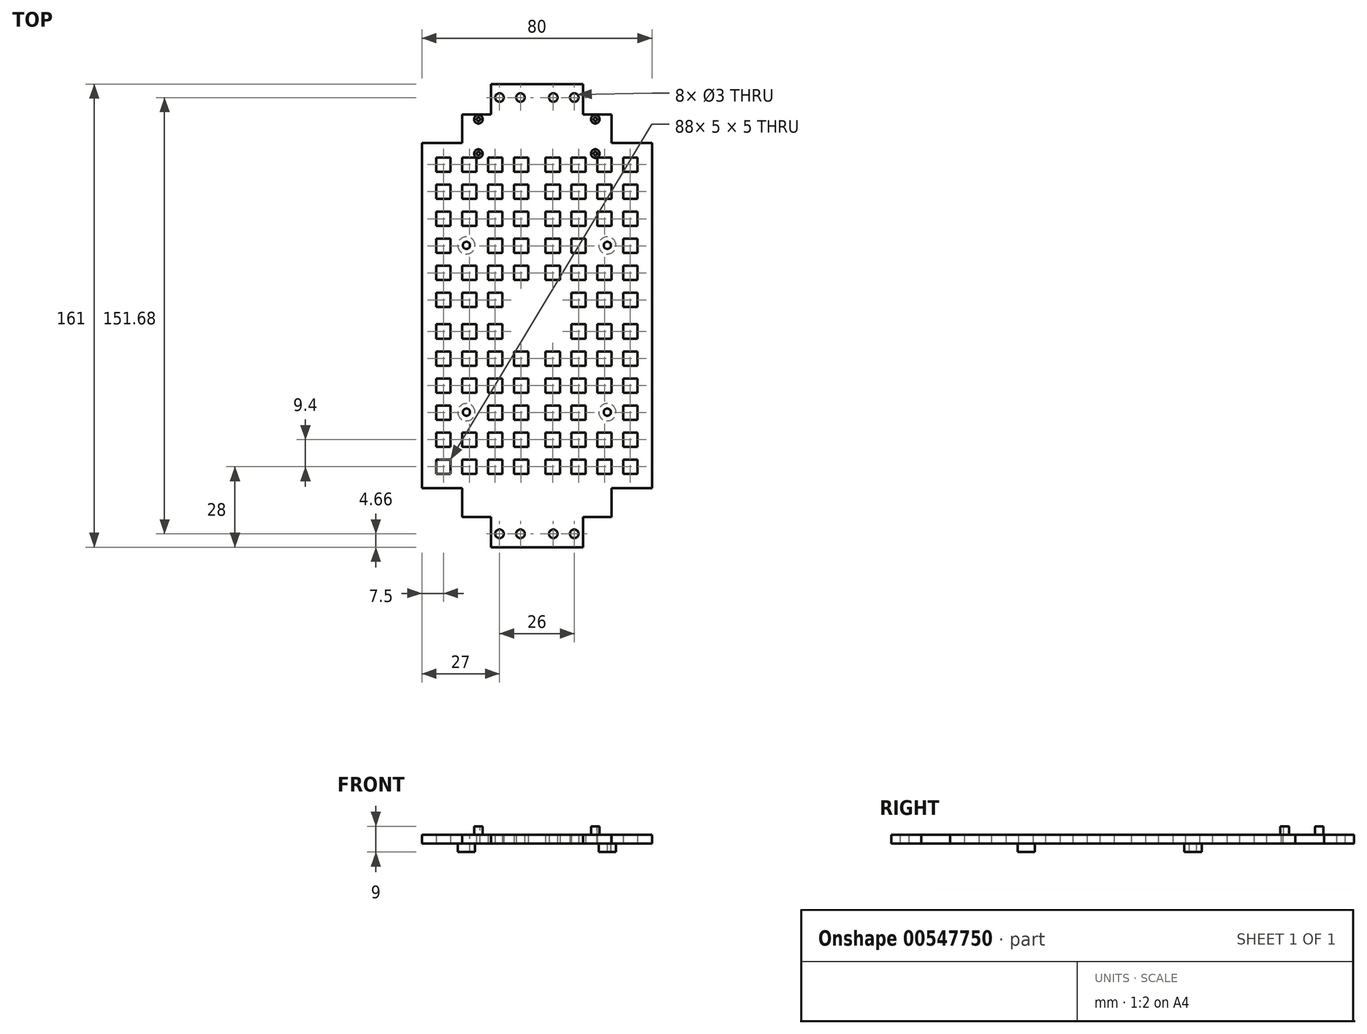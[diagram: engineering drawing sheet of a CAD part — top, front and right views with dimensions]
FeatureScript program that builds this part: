
annotation { "Feature Type Name" : "Feature", "Feature Type Description" : "" }
export const myFeature = defineFeature(function(context is Context, id is Id, definition is map)
    precondition{}
    {
        {
            var Q0;
            Q0=qCreatedBy(makeId("Top.planeOp"),FACE);
            var sketch = newSketch(context, id + "F0", { "sketchPlane" : qUnion([Q0])});
            skLineSegment(sketch, "E0", {"start": v(0, 0) * mm, "end": v(0, 77.06) * mm, "construction": true});
            skLineSegment(sketch, "E1", {"start": v(0, 0) * mm, "end": v(51.76, 0) * mm, "construction": true});
            skLineSegment(sketch, "E2", {"start": v(0, 80.5) * mm, "end": v(16, 80.5) * mm});
            skLineSegment(sketch, "E3", {"start": v(16, 80.5) * mm, "end": v(16, 70) * mm});
            skLineSegment(sketch, "E4", {"start": v(26, 60) * mm, "end": v(40, 60) * mm});
            skLineSegment(sketch, "E5", {"start": v(40, 60) * mm, "end": v(40, 0) * mm});
            skLineSegment(sketch, "E6.MirrorCS", {"start": v(-40, 60) * mm, "end": v(-40, 0) * mm});
            skLineSegment(sketch, "E7.MirrorCS", {"start": v(-26, 60) * mm, "end": v(-40, 60) * mm});
            skLineSegment(sketch, "E8.MirrorCS", {"start": v(0, 80.5) * mm, "end": v(-16, 80.5) * mm});
            skLineSegment(sketch, "E9.MirrorCS", {"start": v(40, -60) * mm, "end": v(40, 0) * mm});
            skLineSegment(sketch, "E10.MirrorCS", {"start": v(-40, -60) * mm, "end": v(-40, 0) * mm});
            skCircle(sketch, "E11", {"center": v(5.7, 75.84) * mm, "radius": 1.5 * mm});
            skCircle(sketch, "E12", {"center": v(13, 75.84) * mm, "radius": 1.5 * mm});
            skLineSegment(sketch, "E13", {"start": v(0, 75.84) * mm, "end": v(16, 75.84) * mm, "construction": true});
            skCircle(sketch, "E14.MirrorC", {"center": v(-13, 75.84) * mm, "radius": 1.5 * mm});
            skCircle(sketch, "E15.MirrorC", {"center": v(-5.7, 75.84) * mm, "radius": 1.5 * mm});
            skLineSegment(sketch, "E16", {"start": v(16, 70) * mm, "end": v(26, 70) * mm});
            skLineSegment(sketch, "E17", {"start": v(26, 70) * mm, "end": v(26, 60) * mm});
            skLineSegment(sketch, "E18.MirrorCS", {"start": v(-26, 70) * mm, "end": v(-26, 60) * mm});
            skLineSegment(sketch, "E19.MirrorCS", {"start": v(-16, 80.5) * mm, "end": v(-16, 70) * mm});
            skLineSegment(sketch, "E20.MirrorCS", {"start": v(-16, 70) * mm, "end": v(-26, 70) * mm});
            skLineSegment(sketch, "E21.MirrorCS", {"start": v(-26, -60) * mm, "end": v(-40, -60) * mm});
            skLineSegment(sketch, "E22.MirrorCS", {"start": v(26, -60) * mm, "end": v(40, -60) * mm});
            skLineSegment(sketch, "E23.MirrorCS", {"start": v(26, -70) * mm, "end": v(26, -60) * mm});
            skLineSegment(sketch, "E24.MirrorCS", {"start": v(16, -70) * mm, "end": v(26, -70) * mm});
            skLineSegment(sketch, "E25.MirrorCS", {"start": v(16, -80.5) * mm, "end": v(16, -70) * mm});
            skLineSegment(sketch, "E26.MirrorCS", {"start": v(0, -80.5) * mm, "end": v(16, -80.5) * mm});
            skLineSegment(sketch, "E27.MirrorCS", {"start": v(0, -80.5) * mm, "end": v(-16, -80.5) * mm});
            skLineSegment(sketch, "E28.MirrorCS", {"start": v(-16, -80.5) * mm, "end": v(-16, -70) * mm});
            skLineSegment(sketch, "E29.MirrorCS", {"start": v(-26, -70) * mm, "end": v(-26, -60) * mm});
            skLineSegment(sketch, "E30.MirrorCS", {"start": v(-16, -70) * mm, "end": v(-26, -70) * mm});
            skCircle(sketch, "E31.MirrorC", {"center": v(13, -75.84) * mm, "radius": 1.5 * mm});
            skCircle(sketch, "E32.MirrorC", {"center": v(5.7, -75.84) * mm, "radius": 1.5 * mm});
            skCircle(sketch, "E33.MirrorC", {"center": v(-13, -75.84) * mm, "radius": 1.5 * mm});
            skCircle(sketch, "E34.MirrorC", {"center": v(-5.7, -75.84) * mm, "radius": 1.5 * mm});
            skLineSegment(sketch, "E35.bottom", {"start": v(35, 50) * mm, "end": v(30, 50) * mm});
            skLineSegment(sketch, "E35.top", {"start": v(35, 55) * mm, "end": v(30, 55) * mm});
            skLineSegment(sketch, "E35.left", {"start": v(35, 50) * mm, "end": v(35, 55) * mm});
            skLineSegment(sketch, "E35.right", {"start": v(30, 50) * mm, "end": v(30, 55) * mm});
            skPoint(sketch, "E35.middle", {"position": v(32.5, 52.5) * mm});
            skPoint(sketch, "E36.1.0.0", {"position": v(23.5, 52.5) * mm});
            skLineSegment(sketch, "E36.1.0.1", {"start": v(26, 55) * mm, "end": v(21, 55) * mm});
            skLineSegment(sketch, "E36.1.0.2", {"start": v(26, 50) * mm, "end": v(21, 50) * mm});
            skLineSegment(sketch, "E36.1.0.3", {"start": v(21, 50) * mm, "end": v(21, 55) * mm});
            skLineSegment(sketch, "E36.1.0.4", {"start": v(26, 50) * mm, "end": v(26, 55) * mm});
            skPoint(sketch, "E36.2.0.0", {"position": v(14.5, 52.5) * mm});
            skLineSegment(sketch, "E36.2.0.1", {"start": v(17, 55) * mm, "end": v(12, 55) * mm});
            skLineSegment(sketch, "E36.2.0.2", {"start": v(17, 50) * mm, "end": v(12, 50) * mm});
            skLineSegment(sketch, "E36.2.0.3", {"start": v(12, 50) * mm, "end": v(12, 55) * mm});
            skLineSegment(sketch, "E36.2.0.4", {"start": v(17, 50) * mm, "end": v(17, 55) * mm});
            skLineSegment(sketch, "E36.direction1", {"start": v(30, 50) * mm, "end": v(21, 50) * mm, "construction": true});
            skPoint(sketch, "E37.0.3.0", {"position": v(5.5, 52.5) * mm});
            skLineSegment(sketch, "E37.1.3.0", {"start": v(8, 55) * mm, "end": v(3, 55) * mm});
            skLineSegment(sketch, "E37.4.3.0", {"start": v(8, 50) * mm, "end": v(3, 50) * mm});
            skLineSegment(sketch, "E37.7.3.0", {"start": v(3, 50) * mm, "end": v(3, 55) * mm});
            skLineSegment(sketch, "E37.10.3.0", {"start": v(8, 50) * mm, "end": v(8, 55) * mm});
            skLineSegment(sketch, "E38.1.0.0", {"start": v(17, 40.6) * mm, "end": v(17, 45.6) * mm});
            skLineSegment(sketch, "E38.1.0.1", {"start": v(3, 40.6) * mm, "end": v(3, 45.6) * mm});
            skLineSegment(sketch, "E38.1.0.2", {"start": v(21, 40.6) * mm, "end": v(21, 45.6) * mm});
            skPoint(sketch, "E38.1.0.3", {"position": v(5.5, 43.1) * mm});
            skLineSegment(sketch, "E38.1.0.4", {"start": v(26, 40.6) * mm, "end": v(26, 45.6) * mm});
            skLineSegment(sketch, "E38.1.0.5", {"start": v(30, 40.6) * mm, "end": v(21, 40.6) * mm, "construction": true});
            skLineSegment(sketch, "E38.1.0.6", {"start": v(35, 45.6) * mm, "end": v(30, 45.6) * mm});
            skLineSegment(sketch, "E38.1.0.7", {"start": v(35, 40.6) * mm, "end": v(35, 45.6) * mm});
            skLineSegment(sketch, "E38.1.0.8", {"start": v(12, 40.6) * mm, "end": v(12, 45.6) * mm});
            skLineSegment(sketch, "E38.1.0.9", {"start": v(17, 40.6) * mm, "end": v(12, 40.6) * mm});
            skPoint(sketch, "E38.1.0.10", {"position": v(23.5, 43.1) * mm});
            skLineSegment(sketch, "E38.1.0.11", {"start": v(8, 40.6) * mm, "end": v(8, 45.6) * mm});
            skLineSegment(sketch, "E38.1.0.12", {"start": v(26, 45.6) * mm, "end": v(21, 45.6) * mm});
            skLineSegment(sketch, "E38.1.0.13", {"start": v(17, 45.6) * mm, "end": v(12, 45.6) * mm});
            skPoint(sketch, "E38.1.0.14", {"position": v(14.5, 43.1) * mm});
            skLineSegment(sketch, "E38.1.0.15", {"start": v(8, 40.6) * mm, "end": v(3, 40.6) * mm});
            skLineSegment(sketch, "E38.1.0.16", {"start": v(35, 40.6) * mm, "end": v(30, 40.6) * mm});
            skPoint(sketch, "E38.1.0.17", {"position": v(32.5, 43.1) * mm});
            skLineSegment(sketch, "E38.1.0.18", {"start": v(8, 45.6) * mm, "end": v(3, 45.6) * mm});
            skLineSegment(sketch, "E38.1.0.19", {"start": v(30, 40.6) * mm, "end": v(30, 45.6) * mm});
            skLineSegment(sketch, "E38.1.0.20", {"start": v(26, 40.6) * mm, "end": v(21, 40.6) * mm});
            skLineSegment(sketch, "E38.2.0.0", {"start": v(17, 31.2) * mm, "end": v(17, 36.2) * mm});
            skLineSegment(sketch, "E38.2.0.1", {"start": v(3, 31.2) * mm, "end": v(3, 36.2) * mm});
            skLineSegment(sketch, "E38.2.0.2", {"start": v(21, 31.2) * mm, "end": v(21, 36.2) * mm});
            skPoint(sketch, "E38.2.0.3", {"position": v(5.5, 33.7) * mm});
            skLineSegment(sketch, "E38.2.0.4", {"start": v(26, 31.2) * mm, "end": v(26, 36.2) * mm});
            skLineSegment(sketch, "E38.2.0.5", {"start": v(30, 31.2) * mm, "end": v(21, 31.2) * mm, "construction": true});
            skLineSegment(sketch, "E38.2.0.6", {"start": v(35, 36.2) * mm, "end": v(30, 36.2) * mm});
            skLineSegment(sketch, "E38.2.0.7", {"start": v(35, 31.2) * mm, "end": v(35, 36.2) * mm});
            skLineSegment(sketch, "E38.2.0.8", {"start": v(12, 31.2) * mm, "end": v(12, 36.2) * mm});
            skLineSegment(sketch, "E38.2.0.9", {"start": v(17, 31.2) * mm, "end": v(12, 31.2) * mm});
            skPoint(sketch, "E38.2.0.10", {"position": v(23.5, 33.7) * mm});
            skLineSegment(sketch, "E38.2.0.11", {"start": v(8, 31.2) * mm, "end": v(8, 36.2) * mm});
            skLineSegment(sketch, "E38.2.0.12", {"start": v(26, 36.2) * mm, "end": v(21, 36.2) * mm});
            skLineSegment(sketch, "E38.2.0.13", {"start": v(17, 36.2) * mm, "end": v(12, 36.2) * mm});
            skPoint(sketch, "E38.2.0.14", {"position": v(14.5, 33.7) * mm});
            skLineSegment(sketch, "E38.2.0.15", {"start": v(8, 31.2) * mm, "end": v(3, 31.2) * mm});
            skLineSegment(sketch, "E38.2.0.16", {"start": v(35, 31.2) * mm, "end": v(30, 31.2) * mm});
            skPoint(sketch, "E38.2.0.17", {"position": v(32.5, 33.7) * mm});
            skLineSegment(sketch, "E38.2.0.18", {"start": v(8, 36.2) * mm, "end": v(3, 36.2) * mm});
            skLineSegment(sketch, "E38.2.0.19", {"start": v(30, 31.2) * mm, "end": v(30, 36.2) * mm});
            skLineSegment(sketch, "E38.2.0.20", {"start": v(26, 31.2) * mm, "end": v(21, 31.2) * mm});
            skLineSegment(sketch, "E38.direction1", {"start": v(3, 50) * mm, "end": v(3, 40.6) * mm, "construction": true});
            skLineSegment(sketch, "E39.0.3.0", {"start": v(17, 21.8) * mm, "end": v(17, 26.8) * mm});
            skLineSegment(sketch, "E39.3.3.0", {"start": v(3, 21.8) * mm, "end": v(3, 26.8) * mm});
            skLineSegment(sketch, "E39.6.3.0", {"start": v(21, 21.8) * mm, "end": v(21, 26.8) * mm, "construction": true});
            skPoint(sketch, "E39.9.3.0", {"position": v(5.5, 24.3) * mm});
            skLineSegment(sketch, "E39.10.3.0", {"start": v(26, 21.8) * mm, "end": v(26, 26.8) * mm, "construction": true});
            skLineSegment(sketch, "E39.13.3.0", {"start": v(30, 21.8) * mm, "end": v(21, 21.8) * mm, "construction": true});
            skLineSegment(sketch, "E39.16.3.0", {"start": v(35, 26.8) * mm, "end": v(30, 26.8) * mm});
            skLineSegment(sketch, "E39.19.3.0", {"start": v(35, 21.8) * mm, "end": v(35, 26.8) * mm});
            skLineSegment(sketch, "E39.22.3.0", {"start": v(12, 21.8) * mm, "end": v(12, 26.8) * mm});
            skLineSegment(sketch, "E39.25.3.0", {"start": v(17, 21.8) * mm, "end": v(12, 21.8) * mm});
            skPoint(sketch, "E39.28.3.0", {"position": v(23.5, 24.3) * mm});
            skLineSegment(sketch, "E39.29.3.0", {"start": v(8, 21.8) * mm, "end": v(8, 26.8) * mm});
            skLineSegment(sketch, "E39.32.3.0", {"start": v(26, 26.8) * mm, "end": v(21, 26.8) * mm, "construction": true});
            skLineSegment(sketch, "E39.35.3.0", {"start": v(17, 26.8) * mm, "end": v(12, 26.8) * mm});
            skPoint(sketch, "E39.38.3.0", {"position": v(14.5, 24.3) * mm});
            skLineSegment(sketch, "E39.39.3.0", {"start": v(8, 21.8) * mm, "end": v(3, 21.8) * mm});
            skLineSegment(sketch, "E39.42.3.0", {"start": v(35, 21.8) * mm, "end": v(30, 21.8) * mm});
            skPoint(sketch, "E39.45.3.0", {"position": v(32.5, 24.3) * mm});
            skLineSegment(sketch, "E39.46.3.0", {"start": v(8, 26.8) * mm, "end": v(3, 26.8) * mm});
            skLineSegment(sketch, "E39.49.3.0", {"start": v(30, 21.8) * mm, "end": v(30, 26.8) * mm});
            skLineSegment(sketch, "E39.52.3.0", {"start": v(26, 21.8) * mm, "end": v(21, 21.8) * mm, "construction": true});
            skLineSegment(sketch, "E39.0.4.0", {"start": v(17, 12.4) * mm, "end": v(17, 17.4) * mm});
            skLineSegment(sketch, "E39.3.4.0", {"start": v(3, 12.4) * mm, "end": v(3, 17.4) * mm});
            skLineSegment(sketch, "E39.6.4.0", {"start": v(21, 12.4) * mm, "end": v(21, 17.4) * mm});
            skPoint(sketch, "E39.9.4.0", {"position": v(5.5, 14.9) * mm});
            skLineSegment(sketch, "E39.10.4.0", {"start": v(26, 12.4) * mm, "end": v(26, 17.4) * mm});
            skLineSegment(sketch, "E39.13.4.0", {"start": v(30, 12.4) * mm, "end": v(21, 12.4) * mm, "construction": true});
            skLineSegment(sketch, "E39.16.4.0", {"start": v(35, 17.4) * mm, "end": v(30, 17.4) * mm});
            skLineSegment(sketch, "E39.19.4.0", {"start": v(35, 12.4) * mm, "end": v(35, 17.4) * mm});
            skLineSegment(sketch, "E39.22.4.0", {"start": v(12, 12.4) * mm, "end": v(12, 17.4) * mm});
            skLineSegment(sketch, "E39.25.4.0", {"start": v(17, 12.4) * mm, "end": v(12, 12.4) * mm});
            skPoint(sketch, "E39.28.4.0", {"position": v(23.5, 14.9) * mm});
            skLineSegment(sketch, "E39.29.4.0", {"start": v(8, 12.4) * mm, "end": v(8, 17.4) * mm});
            skLineSegment(sketch, "E39.32.4.0", {"start": v(26, 17.4) * mm, "end": v(21, 17.4) * mm});
            skLineSegment(sketch, "E39.35.4.0", {"start": v(17, 17.4) * mm, "end": v(12, 17.4) * mm});
            skPoint(sketch, "E39.38.4.0", {"position": v(14.5, 14.9) * mm});
            skLineSegment(sketch, "E39.39.4.0", {"start": v(8, 12.4) * mm, "end": v(3, 12.4) * mm});
            skLineSegment(sketch, "E39.42.4.0", {"start": v(35, 12.4) * mm, "end": v(30, 12.4) * mm});
            skPoint(sketch, "E39.45.4.0", {"position": v(32.5, 14.9) * mm});
            skLineSegment(sketch, "E39.46.4.0", {"start": v(8, 17.4) * mm, "end": v(3, 17.4) * mm});
            skLineSegment(sketch, "E39.49.4.0", {"start": v(30, 12.4) * mm, "end": v(30, 17.4) * mm});
            skLineSegment(sketch, "E39.52.4.0", {"start": v(26, 12.4) * mm, "end": v(21, 12.4) * mm});
            skLineSegment(sketch, "E39.0.5.0", {"start": v(17, 3) * mm, "end": v(17, 8) * mm});
            skLineSegment(sketch, "E39.3.5.0", {"start": v(3, 3) * mm, "end": v(3, 8) * mm, "construction": true});
            skLineSegment(sketch, "E39.6.5.0", {"start": v(21, 3) * mm, "end": v(21, 8) * mm});
            skPoint(sketch, "E39.9.5.0", {"position": v(5.5, 5.5) * mm});
            skLineSegment(sketch, "E39.10.5.0", {"start": v(26, 3) * mm, "end": v(26, 8) * mm});
            skLineSegment(sketch, "E39.13.5.0", {"start": v(30, 3) * mm, "end": v(21, 3) * mm, "construction": true});
            skLineSegment(sketch, "E39.16.5.0", {"start": v(35, 8) * mm, "end": v(30, 8) * mm});
            skLineSegment(sketch, "E39.19.5.0", {"start": v(35, 3) * mm, "end": v(35, 8) * mm});
            skLineSegment(sketch, "E39.22.5.0", {"start": v(12, 3) * mm, "end": v(12, 8) * mm});
            skLineSegment(sketch, "E39.25.5.0", {"start": v(17, 3) * mm, "end": v(12, 3) * mm});
            skPoint(sketch, "E39.28.5.0", {"position": v(23.5, 5.5) * mm});
            skLineSegment(sketch, "E39.29.5.0", {"start": v(8, 3) * mm, "end": v(8, 8) * mm, "construction": true});
            skLineSegment(sketch, "E39.32.5.0", {"start": v(26, 8) * mm, "end": v(21, 8) * mm});
            skLineSegment(sketch, "E39.35.5.0", {"start": v(17, 8) * mm, "end": v(12, 8) * mm});
            skPoint(sketch, "E39.38.5.0", {"position": v(14.5, 5.5) * mm});
            skLineSegment(sketch, "E39.39.5.0", {"start": v(8, 3) * mm, "end": v(3, 3) * mm, "construction": true});
            skLineSegment(sketch, "E39.42.5.0", {"start": v(35, 3) * mm, "end": v(30, 3) * mm});
            skPoint(sketch, "E39.45.5.0", {"position": v(32.5, 5.5) * mm});
            skLineSegment(sketch, "E39.46.5.0", {"start": v(8, 8) * mm, "end": v(3, 8) * mm, "construction": true});
            skLineSegment(sketch, "E39.49.5.0", {"start": v(30, 3) * mm, "end": v(30, 8) * mm});
            skLineSegment(sketch, "E39.52.5.0", {"start": v(26, 3) * mm, "end": v(21, 3) * mm});
            skLineSegment(sketch, "E40.MirrorCS", {"start": v(-26, 3) * mm, "end": v(-21, 3) * mm});
            skLineSegment(sketch, "E41.MirrorCS", {"start": v(-35, 45.6) * mm, "end": v(-30, 45.6) * mm});
            skLineSegment(sketch, "E42.MirrorCS", {"start": v(-26, 12.4) * mm, "end": v(-21, 12.4) * mm});
            skLineSegment(sketch, "E43.MirrorCS", {"start": v(-26, 50) * mm, "end": v(-21, 50) * mm});
            skLineSegment(sketch, "E44.MirrorCS", {"start": v(-26, 21.8) * mm, "end": v(-21, 21.8) * mm, "construction": true});
            skLineSegment(sketch, "E45.MirrorCS", {"start": v(-3, 40.6) * mm, "end": v(-3, 45.6) * mm});
            skLineSegment(sketch, "E46.MirrorCS", {"start": v(-26, 31.2) * mm, "end": v(-21, 31.2) * mm});
            skLineSegment(sketch, "E47.MirrorCS", {"start": v(-26, 40.6) * mm, "end": v(-21, 40.6) * mm});
            skPoint(sketch, "E48.MirrorP", {"position": v(-14.5, 52.5) * mm});
            skPoint(sketch, "E49.MirrorP", {"position": v(-14.5, 14.9) * mm});
            skLineSegment(sketch, "E50.MirrorCS", {"start": v(-30, 3) * mm, "end": v(-21, 3) * mm, "construction": true});
            skLineSegment(sketch, "E51.MirrorCS", {"start": v(-35, 17.4) * mm, "end": v(-30, 17.4) * mm});
            skLineSegment(sketch, "E52.MirrorCS", {"start": v(-8, 40.6) * mm, "end": v(-8, 45.6) * mm});
            skLineSegment(sketch, "E53.MirrorCS", {"start": v(-12, 50) * mm, "end": v(-12, 55) * mm});
            skPoint(sketch, "E54.MirrorP", {"position": v(-23.5, 52.5) * mm});
            skLineSegment(sketch, "E55.MirrorCS", {"start": v(-17, 31.2) * mm, "end": v(-12, 31.2) * mm});
            skPoint(sketch, "E56.MirrorP", {"position": v(-23.5, 14.9) * mm});
            skLineSegment(sketch, "E57.MirrorCS", {"start": v(-35, 21.8) * mm, "end": v(-35, 26.8) * mm});
            skLineSegment(sketch, "E58.MirrorCS", {"start": v(-26, 8) * mm, "end": v(-21, 8) * mm});
            skLineSegment(sketch, "E59.MirrorCS", {"start": v(-8, 36.2) * mm, "end": v(-3, 36.2) * mm});
            skLineSegment(sketch, "E60.MirrorCS", {"start": v(-30, 40.6) * mm, "end": v(-30, 45.6) * mm});
            skPoint(sketch, "E61.MirrorP", {"position": v(-32.5, 43.1) * mm});
            skLineSegment(sketch, "E62.MirrorCS", {"start": v(-17, 17.4) * mm, "end": v(-12, 17.4) * mm});
            skLineSegment(sketch, "E63.MirrorCS", {"start": v(-35, 50) * mm, "end": v(-30, 50) * mm});
            skLineSegment(sketch, "E64.MirrorCS", {"start": v(-8, 50) * mm, "end": v(-8, 55) * mm});
            skPoint(sketch, "E65.MirrorP", {"position": v(-32.5, 5.5) * mm});
            skLineSegment(sketch, "E66.MirrorCS", {"start": v(-17, 26.8) * mm, "end": v(-12, 26.8) * mm});
            skLineSegment(sketch, "E67.MirrorCS", {"start": v(-8, 45.6) * mm, "end": v(-3, 45.6) * mm});
            skLineSegment(sketch, "E68.MirrorCS", {"start": v(-3, 50) * mm, "end": v(-3, 55) * mm});
            skLineSegment(sketch, "E69.MirrorCS", {"start": v(-8, 3) * mm, "end": v(-8, 8) * mm, "construction": true});
            skPoint(sketch, "E70.MirrorP", {"position": v(-14.5, 5.5) * mm});
            skPoint(sketch, "E71.MirrorP", {"position": v(-14.5, 43.1) * mm});
            skLineSegment(sketch, "E72.MirrorCS", {"start": v(-35, 31.2) * mm, "end": v(-30, 31.2) * mm});
            skLineSegment(sketch, "E73.MirrorCS", {"start": v(-26, 17.4) * mm, "end": v(-21, 17.4) * mm});
            skLineSegment(sketch, "E74.MirrorCS", {"start": v(-17, 3) * mm, "end": v(-12, 3) * mm});
            skLineSegment(sketch, "E75.MirrorCS", {"start": v(-26, 26.8) * mm, "end": v(-21, 26.8) * mm, "construction": true});
            skLineSegment(sketch, "E76.MirrorCS", {"start": v(-8, 12.4) * mm, "end": v(-8, 17.4) * mm});
            skLineSegment(sketch, "E77.MirrorCS", {"start": v(-35, 40.6) * mm, "end": v(-30, 40.6) * mm});
            skLineSegment(sketch, "E78.MirrorCS", {"start": v(-8, 50) * mm, "end": v(-3, 50) * mm});
            skLineSegment(sketch, "E79.MirrorCS", {"start": v(-8, 31.2) * mm, "end": v(-3, 31.2) * mm});
            skPoint(sketch, "E80.MirrorP", {"position": v(-23.5, 43.1) * mm});
            skPoint(sketch, "E81.MirrorP", {"position": v(-23.5, 5.5) * mm});
            skLineSegment(sketch, "E82.MirrorCS", {"start": v(-30, 12.4) * mm, "end": v(-21, 12.4) * mm, "construction": true});
            skLineSegment(sketch, "E83.MirrorCS", {"start": v(-35, 26.8) * mm, "end": v(-30, 26.8) * mm});
            skLineSegment(sketch, "E84.MirrorCS", {"start": v(-17, 40.6) * mm, "end": v(-12, 40.6) * mm});
            skLineSegment(sketch, "E85.MirrorCS", {"start": v(-12, 31.2) * mm, "end": v(-12, 36.2) * mm});
            skLineSegment(sketch, "E86.MirrorCS", {"start": v(-26, 3) * mm, "end": v(-26, 8) * mm});
            skLineSegment(sketch, "E87.MirrorCS", {"start": v(-17, 50) * mm, "end": v(-12, 50) * mm});
            skPoint(sketch, "E88.MirrorP", {"position": v(-5.5, 14.9) * mm});
            skPoint(sketch, "E89.MirrorP", {"position": v(-32.5, 52.5) * mm});
            skPoint(sketch, "E90.MirrorP", {"position": v(-32.5, 24.3) * mm});
            skPoint(sketch, "E91.MirrorP", {"position": v(-14.5, 24.3) * mm});
            skLineSegment(sketch, "E92.MirrorCS", {"start": v(-35, 31.2) * mm, "end": v(-35, 36.2) * mm});
            skLineSegment(sketch, "E93.MirrorCS", {"start": v(-26, 12.4) * mm, "end": v(-26, 17.4) * mm});
            skLineSegment(sketch, "E94.MirrorCS", {"start": v(-30, 21.8) * mm, "end": v(-21, 21.8) * mm, "construction": true});
            skLineSegment(sketch, "E95.MirrorCS", {"start": v(-17, 55) * mm, "end": v(-12, 55) * mm});
            skLineSegment(sketch, "E96.MirrorCS", {"start": v(-21, 3) * mm, "end": v(-21, 8) * mm});
            skLineSegment(sketch, "E97.MirrorCS", {"start": v(-3, 3) * mm, "end": v(-3, 8) * mm, "construction": true});
            skLineSegment(sketch, "E98.MirrorCS", {"start": v(-35, 36.2) * mm, "end": v(-30, 36.2) * mm});
            skLineSegment(sketch, "E99.MirrorCS", {"start": v(-35, 40.6) * mm, "end": v(-35, 45.6) * mm});
            skLineSegment(sketch, "E100.MirrorCS", {"start": v(-26, 50) * mm, "end": v(-26, 55) * mm});
            skLineSegment(sketch, "E101.MirrorCS", {"start": v(-12, 40.6) * mm, "end": v(-12, 45.6) * mm});
            skLineSegment(sketch, "E102.MirrorCS", {"start": v(-26, 21.8) * mm, "end": v(-26, 26.8) * mm, "construction": true});
            skLineSegment(sketch, "E103.MirrorCS", {"start": v(-21, 12.4) * mm, "end": v(-21, 17.4) * mm});
            skLineSegment(sketch, "E104.MirrorCS", {"start": v(-8, 55) * mm, "end": v(-3, 55) * mm});
            skLineSegment(sketch, "E105.MirrorCS", {"start": v(-30, 31.2) * mm, "end": v(-21, 31.2) * mm, "construction": true});
            skLineSegment(sketch, "E106.MirrorCS", {"start": v(-17, 3) * mm, "end": v(-17, 8) * mm});
            skLineSegment(sketch, "E107.MirrorCS", {"start": v(-3, 12.4) * mm, "end": v(-3, 17.4) * mm});
            skLineSegment(sketch, "E108.MirrorCS", {"start": v(-21, 21.8) * mm, "end": v(-21, 26.8) * mm, "construction": true});
            skLineSegment(sketch, "E109.MirrorCS", {"start": v(-8, 40.6) * mm, "end": v(-3, 40.6) * mm});
            skPoint(sketch, "E110.MirrorP", {"position": v(-5.5, 5.5) * mm});
            skPoint(sketch, "E111.MirrorP", {"position": v(-5.5, 43.1) * mm});
            skLineSegment(sketch, "E112.MirrorCS", {"start": v(-17, 36.2) * mm, "end": v(-12, 36.2) * mm});
            skLineSegment(sketch, "E113.MirrorCS", {"start": v(-21, 50) * mm, "end": v(-21, 55) * mm});
            skPoint(sketch, "E114.MirrorP", {"position": v(-23.5, 24.3) * mm});
            skPoint(sketch, "E115.MirrorP", {"position": v(-5.5, 24.3) * mm});
            skLineSegment(sketch, "E116.MirrorCS", {"start": v(-17, 12.4) * mm, "end": v(-12, 12.4) * mm});
            skLineSegment(sketch, "E117.MirrorCS", {"start": v(-8, 21.8) * mm, "end": v(-8, 26.8) * mm});
            skLineSegment(sketch, "E118.MirrorCS", {"start": v(-30, 40.6) * mm, "end": v(-21, 40.6) * mm, "construction": true});
            skLineSegment(sketch, "E119.MirrorCS", {"start": v(-30, 3) * mm, "end": v(-30, 8) * mm});
            skLineSegment(sketch, "E120.MirrorCS", {"start": v(-17, 12.4) * mm, "end": v(-17, 17.4) * mm});
            skLineSegment(sketch, "E121.MirrorCS", {"start": v(-26, 31.2) * mm, "end": v(-26, 36.2) * mm});
            skLineSegment(sketch, "E122.MirrorCS", {"start": v(-26, 55) * mm, "end": v(-21, 55) * mm});
            skLineSegment(sketch, "E123.MirrorCS", {"start": v(-3, 21.8) * mm, "end": v(-3, 26.8) * mm});
            skLineSegment(sketch, "E124.MirrorCS", {"start": v(-8, 8) * mm, "end": v(-3, 8) * mm, "construction": true});
            skLineSegment(sketch, "E125.MirrorCS", {"start": v(-12, 3) * mm, "end": v(-12, 8) * mm});
            skLineSegment(sketch, "E126.MirrorCS", {"start": v(-30, 12.4) * mm, "end": v(-30, 17.4) * mm});
            skLineSegment(sketch, "E127.MirrorCS", {"start": v(-17, 21.8) * mm, "end": v(-17, 26.8) * mm});
            skLineSegment(sketch, "E128.MirrorCS", {"start": v(-8, 17.4) * mm, "end": v(-3, 17.4) * mm});
            skLineSegment(sketch, "E129.MirrorCS", {"start": v(-30, 50) * mm, "end": v(-21, 50) * mm, "construction": true});
            skLineSegment(sketch, "E130.MirrorCS", {"start": v(-3, 50) * mm, "end": v(-3, 40.6) * mm, "construction": true});
            skLineSegment(sketch, "E131.MirrorCS", {"start": v(-21, 40.6) * mm, "end": v(-21, 45.6) * mm});
            skLineSegment(sketch, "E132.MirrorCS", {"start": v(-30, 50) * mm, "end": v(-30, 55) * mm});
            skLineSegment(sketch, "E133.MirrorCS", {"start": v(-21, 31.2) * mm, "end": v(-21, 36.2) * mm});
            skLineSegment(sketch, "E134.MirrorCS", {"start": v(-30, 21.8) * mm, "end": v(-30, 26.8) * mm});
            skLineSegment(sketch, "E135.MirrorCS", {"start": v(-3, 31.2) * mm, "end": v(-3, 36.2) * mm});
            skLineSegment(sketch, "E136.MirrorCS", {"start": v(-35, 3) * mm, "end": v(-30, 3) * mm});
            skLineSegment(sketch, "E137.MirrorCS", {"start": v(-26, 40.6) * mm, "end": v(-26, 45.6) * mm});
            skPoint(sketch, "E138.MirrorP", {"position": v(-32.5, 33.7) * mm});
            skLineSegment(sketch, "E139.MirrorCS", {"start": v(-35, 3) * mm, "end": v(-35, 8) * mm});
            skLineSegment(sketch, "E140.MirrorCS", {"start": v(-12, 12.4) * mm, "end": v(-12, 17.4) * mm});
            skLineSegment(sketch, "E141.MirrorCS", {"start": v(-17, 21.8) * mm, "end": v(-12, 21.8) * mm});
            skPoint(sketch, "E142.MirrorP", {"position": v(-14.5, 33.7) * mm});
            skLineSegment(sketch, "E143.MirrorCS", {"start": v(-8, 3) * mm, "end": v(-3, 3) * mm, "construction": true});
            skLineSegment(sketch, "E144.MirrorCS", {"start": v(-17, 31.2) * mm, "end": v(-17, 36.2) * mm});
            skLineSegment(sketch, "E145.MirrorCS", {"start": v(-35, 12.4) * mm, "end": v(-30, 12.4) * mm});
            skLineSegment(sketch, "E146.MirrorCS", {"start": v(-35, 50) * mm, "end": v(-35, 55) * mm});
            skLineSegment(sketch, "E147.MirrorCS", {"start": v(-8, 26.8) * mm, "end": v(-3, 26.8) * mm});
            skLineSegment(sketch, "E148.MirrorCS", {"start": v(-17, 45.6) * mm, "end": v(-12, 45.6) * mm});
            skLineSegment(sketch, "E149.MirrorCS", {"start": v(-26, 36.2) * mm, "end": v(-21, 36.2) * mm});
            skLineSegment(sketch, "E150.MirrorCS", {"start": v(-8, 21.8) * mm, "end": v(-3, 21.8) * mm});
            skPoint(sketch, "E151.MirrorP", {"position": v(-5.5, 52.5) * mm});
            skPoint(sketch, "E152.MirrorP", {"position": v(-32.5, 14.9) * mm});
            skPoint(sketch, "E153.MirrorP", {"position": v(-23.5, 33.7) * mm});
            skLineSegment(sketch, "E154.MirrorCS", {"start": v(-17, 8) * mm, "end": v(-12, 8) * mm});
            skLineSegment(sketch, "E155.MirrorCS", {"start": v(-17, 40.6) * mm, "end": v(-17, 45.6) * mm});
            skLineSegment(sketch, "E156.MirrorCS", {"start": v(-35, 55) * mm, "end": v(-30, 55) * mm});
            skPoint(sketch, "E157.MirrorP", {"position": v(-5.5, 33.7) * mm});
            skLineSegment(sketch, "E158.MirrorCS", {"start": v(-8, 12.4) * mm, "end": v(-3, 12.4) * mm});
            skLineSegment(sketch, "E159.MirrorCS", {"start": v(-35, 21.8) * mm, "end": v(-30, 21.8) * mm});
            skLineSegment(sketch, "E160.MirrorCS", {"start": v(-30, 31.2) * mm, "end": v(-30, 36.2) * mm});
            skLineSegment(sketch, "E161.MirrorCS", {"start": v(-35, 12.4) * mm, "end": v(-35, 17.4) * mm});
            skLineSegment(sketch, "E162.MirrorCS", {"start": v(-35, 8) * mm, "end": v(-30, 8) * mm});
            skLineSegment(sketch, "E163.MirrorCS", {"start": v(-17, 50) * mm, "end": v(-17, 55) * mm});
            skLineSegment(sketch, "E164.MirrorCS", {"start": v(-12, 21.8) * mm, "end": v(-12, 26.8) * mm});
            skLineSegment(sketch, "E165.MirrorCS", {"start": v(-26, 45.6) * mm, "end": v(-21, 45.6) * mm});
            skLineSegment(sketch, "E166.MirrorCS", {"start": v(-8, 31.2) * mm, "end": v(-8, 36.2) * mm});
            skLineSegment(sketch, "E167.MirrorCS", {"start": v(-26, -31.2) * mm, "end": v(-21, -31.2) * mm, "construction": true});
            skLineSegment(sketch, "E168.MirrorCS", {"start": v(-26, -50) * mm, "end": v(-21, -50) * mm});
            skLineSegment(sketch, "E169.MirrorCS", {"start": v(-26, -40.6) * mm, "end": v(-21, -40.6) * mm});
            skLineSegment(sketch, "E170.MirrorCS", {"start": v(26, -40.6) * mm, "end": v(21, -40.6) * mm});
            skLineSegment(sketch, "E171.MirrorCS", {"start": v(26, -31.2) * mm, "end": v(21, -31.2) * mm, "construction": true});
            skLineSegment(sketch, "E172.MirrorCS", {"start": v(3, -40.6) * mm, "end": v(3, -45.6) * mm});
            skLineSegment(sketch, "E173.MirrorCS", {"start": v(26, -50) * mm, "end": v(21, -50) * mm});
            skLineSegment(sketch, "E174.MirrorCS", {"start": v(26, -12.4) * mm, "end": v(21, -12.4) * mm});
            skLineSegment(sketch, "E175.MirrorCS", {"start": v(26, -21.8) * mm, "end": v(21, -21.8) * mm});
            skLineSegment(sketch, "E176.MirrorCS", {"start": v(35, -45.6) * mm, "end": v(30, -45.6) * mm});
            skLineSegment(sketch, "E177.MirrorCS", {"start": v(-26, -3) * mm, "end": v(-21, -3) * mm});
            skLineSegment(sketch, "E178.MirrorCS", {"start": v(-26, -21.8) * mm, "end": v(-21, -21.8) * mm});
            skLineSegment(sketch, "E179.MirrorCS", {"start": v(26, -3) * mm, "end": v(21, -3) * mm});
            skLineSegment(sketch, "E180.MirrorCS", {"start": v(-3, -40.6) * mm, "end": v(-3, -45.6) * mm});
            skLineSegment(sketch, "E181.MirrorCS", {"start": v(-26, -12.4) * mm, "end": v(-21, -12.4) * mm});
            skLineSegment(sketch, "E182.MirrorCS", {"start": v(30, -31.2) * mm, "end": v(21, -31.2) * mm, "construction": true});
            skPoint(sketch, "E183.MirrorP", {"position": v(-23.5, -5.5) * mm});
            skLineSegment(sketch, "E184.MirrorCS", {"start": v(26, -36.2) * mm, "end": v(21, -36.2) * mm, "construction": true});
            skPoint(sketch, "E185.MirrorP", {"position": v(-23.5, -43.1) * mm});
            skLineSegment(sketch, "E186.MirrorCS", {"start": v(-26, -31.2) * mm, "end": v(-26, -36.2) * mm, "construction": true});
            skPoint(sketch, "E187.MirrorP", {"position": v(23.5, -5.5) * mm});
            skLineSegment(sketch, "E188.MirrorCS", {"start": v(17, -21.8) * mm, "end": v(12, -21.8) * mm});
            skLineSegment(sketch, "E189.MirrorCS", {"start": v(26, -12.4) * mm, "end": v(26, -17.4) * mm});
            skLineSegment(sketch, "E190.MirrorCS", {"start": v(-21, -12.4) * mm, "end": v(-21, -17.4) * mm});
            skPoint(sketch, "E191.MirrorP", {"position": v(23.5, -14.9) * mm});
            skLineSegment(sketch, "E192.MirrorCS", {"start": v(30, -21.8) * mm, "end": v(21, -21.8) * mm, "construction": true});
            skLineSegment(sketch, "E193.MirrorCS", {"start": v(-35, -12.4) * mm, "end": v(-35, -17.4) * mm});
            skLineSegment(sketch, "E194.MirrorCS", {"start": v(-35, -45.6) * mm, "end": v(-30, -45.6) * mm});
            skLineSegment(sketch, "E195.MirrorCS", {"start": v(-3, -50) * mm, "end": v(-3, -55) * mm});
            skLineSegment(sketch, "E196.MirrorCS", {"start": v(-8, -17.4) * mm, "end": v(-3, -17.4) * mm});
            skLineSegment(sketch, "E197.MirrorCS", {"start": v(-21, -21.8) * mm, "end": v(-21, -26.8) * mm});
            skLineSegment(sketch, "E198.MirrorCS", {"start": v(-35, -31.2) * mm, "end": v(-35, -36.2) * mm});
            skLineSegment(sketch, "E199.MirrorCS", {"start": v(8, -21.8) * mm, "end": v(8, -26.8) * mm});
            skLineSegment(sketch, "E200.MirrorCS", {"start": v(17, -12.4) * mm, "end": v(12, -12.4) * mm});
            skPoint(sketch, "E201.MirrorP", {"position": v(-5.5, -5.5) * mm});
            skLineSegment(sketch, "E202.MirrorCS", {"start": v(17, -50) * mm, "end": v(12, -50) * mm});
            skPoint(sketch, "E203.MirrorP", {"position": v(14.5, -5.5) * mm});
            skLineSegment(sketch, "E204.MirrorCS", {"start": v(17, -40.6) * mm, "end": v(12, -40.6) * mm});
            skLineSegment(sketch, "E205.MirrorCS", {"start": v(17, -55) * mm, "end": v(12, -55) * mm});
            skLineSegment(sketch, "E206.MirrorCS", {"start": v(-8, -31.2) * mm, "end": v(-8, -36.2) * mm});
            skPoint(sketch, "E207.MirrorP", {"position": v(-5.5, -14.9) * mm});
            skLineSegment(sketch, "E208.MirrorCS", {"start": v(30, -12.4) * mm, "end": v(21, -12.4) * mm, "construction": true});
            skLineSegment(sketch, "E209.MirrorCS", {"start": v(26, -3) * mm, "end": v(26, -8) * mm});
            skLineSegment(sketch, "E210.MirrorCS", {"start": v(12, -3) * mm, "end": v(12, -8) * mm});
            skLineSegment(sketch, "E211.MirrorCS", {"start": v(-12, -3) * mm, "end": v(-12, -8) * mm});
            skLineSegment(sketch, "E212.MirrorCS", {"start": v(-17, -21.8) * mm, "end": v(-12, -21.8) * mm});
            skLineSegment(sketch, "E213.MirrorCS", {"start": v(-17, -45.6) * mm, "end": v(-12, -45.6) * mm});
            skLineSegment(sketch, "E214.MirrorCS", {"start": v(-8, -3) * mm, "end": v(-3, -3) * mm, "construction": true});
            skLineSegment(sketch, "E215.MirrorCS", {"start": v(-12, -31.2) * mm, "end": v(-12, -36.2) * mm});
            skLineSegment(sketch, "E216.MirrorCS", {"start": v(-17, -50) * mm, "end": v(-17, -55) * mm});
            skLineSegment(sketch, "E217.MirrorCS", {"start": v(-8, -50) * mm, "end": v(-8, -55) * mm});
            skLineSegment(sketch, "E218.MirrorCS", {"start": v(-30, -31.2) * mm, "end": v(-21, -31.2) * mm, "construction": true});
            skPoint(sketch, "E219.MirrorP", {"position": v(32.5, -14.9) * mm});
            skLineSegment(sketch, "E220.MirrorCS", {"start": v(35, -17.4) * mm, "end": v(30, -17.4) * mm});
            skPoint(sketch, "E221.MirrorP", {"position": v(-32.5, -52.5) * mm});
            skLineSegment(sketch, "E222.MirrorCS", {"start": v(35, -21.8) * mm, "end": v(35, -26.8) * mm});
            skLineSegment(sketch, "E223.MirrorCS", {"start": v(30, -3) * mm, "end": v(21, -3) * mm, "construction": true});
            skLineSegment(sketch, "E224.MirrorCS", {"start": v(12, -50) * mm, "end": v(12, -55) * mm});
            skPoint(sketch, "E225.MirrorP", {"position": v(5.5, -52.5) * mm});
            skLineSegment(sketch, "E226.MirrorCS", {"start": v(8, -40.6) * mm, "end": v(8, -45.6) * mm});
            skLineSegment(sketch, "E227.MirrorCS", {"start": v(17, -31.2) * mm, "end": v(12, -31.2) * mm});
            skLineSegment(sketch, "E228.MirrorCS", {"start": v(8, -12.4) * mm, "end": v(8, -17.4) * mm});
            skLineSegment(sketch, "E229.MirrorCS", {"start": v(17, -3) * mm, "end": v(12, -3) * mm});
            skLineSegment(sketch, "E230.MirrorCS", {"start": v(8, -50) * mm, "end": v(3, -50) * mm});
            skPoint(sketch, "E231.MirrorP", {"position": v(32.5, -5.5) * mm});
            skLineSegment(sketch, "E232.MirrorCS", {"start": v(26, -26.8) * mm, "end": v(21, -26.8) * mm});
            skPoint(sketch, "E233.MirrorP", {"position": v(-5.5, -43.1) * mm});
            skPoint(sketch, "E234.MirrorP", {"position": v(32.5, -43.1) * mm});
            skLineSegment(sketch, "E235.MirrorCS", {"start": v(35, -40.6) * mm, "end": v(30, -40.6) * mm});
            skLineSegment(sketch, "E236.MirrorCS", {"start": v(8, -31.2) * mm, "end": v(3, -31.2) * mm});
            skLineSegment(sketch, "E237.MirrorCS", {"start": v(-17, -26.8) * mm, "end": v(-12, -26.8) * mm});
            skLineSegment(sketch, "E238.MirrorCS", {"start": v(-8, -3) * mm, "end": v(-8, -8) * mm, "construction": true});
            skLineSegment(sketch, "E239.MirrorCS", {"start": v(-8, -26.8) * mm, "end": v(-3, -26.8) * mm});
            skLineSegment(sketch, "E240.MirrorCS", {"start": v(-8, -40.6) * mm, "end": v(-3, -40.6) * mm});
            skLineSegment(sketch, "E241.MirrorCS", {"start": v(-26, -12.4) * mm, "end": v(-26, -17.4) * mm});
            skLineSegment(sketch, "E242.MirrorCS", {"start": v(-30, -50) * mm, "end": v(-21, -50) * mm, "construction": true});
            skLineSegment(sketch, "E243.MirrorCS", {"start": v(26, -21.8) * mm, "end": v(26, -26.8) * mm});
            skLineSegment(sketch, "E244.MirrorCS", {"start": v(8, -55) * mm, "end": v(3, -55) * mm});
            skLineSegment(sketch, "E245.MirrorCS", {"start": v(8, -40.6) * mm, "end": v(3, -40.6) * mm});
            skPoint(sketch, "E246.MirrorP", {"position": v(14.5, -43.1) * mm});
            skLineSegment(sketch, "E247.MirrorCS", {"start": v(-17, -17.4) * mm, "end": v(-12, -17.4) * mm});
            skLineSegment(sketch, "E248.MirrorCS", {"start": v(35, -31.2) * mm, "end": v(30, -31.2) * mm});
            skLineSegment(sketch, "E249.MirrorCS", {"start": v(3, -50) * mm, "end": v(3, -55) * mm});
            skLineSegment(sketch, "E250.MirrorCS", {"start": v(8, -45.6) * mm, "end": v(3, -45.6) * mm});
            skPoint(sketch, "E251.MirrorP", {"position": v(5.5, -33.7) * mm});
            skLineSegment(sketch, "E252.MirrorCS", {"start": v(26, -17.4) * mm, "end": v(21, -17.4) * mm});
            skLineSegment(sketch, "E253.MirrorCS", {"start": v(-30, -3) * mm, "end": v(-21, -3) * mm, "construction": true});
            skLineSegment(sketch, "E254.MirrorCS", {"start": v(-30, -21.8) * mm, "end": v(-21, -21.8) * mm, "construction": true});
            skLineSegment(sketch, "E255.MirrorCS", {"start": v(17, -26.8) * mm, "end": v(12, -26.8) * mm});
            skLineSegment(sketch, "E256.MirrorCS", {"start": v(-17, -36.2) * mm, "end": v(-12, -36.2) * mm});
            skLineSegment(sketch, "E257.MirrorCS", {"start": v(8, -3) * mm, "end": v(8, -8) * mm, "construction": true});
            skLineSegment(sketch, "E258.MirrorCS", {"start": v(-35, -31.2) * mm, "end": v(-30, -31.2) * mm});
            skLineSegment(sketch, "E259.MirrorCS", {"start": v(-3, -50) * mm, "end": v(-3, -40.6) * mm, "construction": true});
            skPoint(sketch, "E260.MirrorP", {"position": v(-14.5, -52.5) * mm});
            skPoint(sketch, "E261.MirrorP", {"position": v(-23.5, -24.3) * mm});
            skPoint(sketch, "E262.MirrorP", {"position": v(-5.5, -24.3) * mm});
            skLineSegment(sketch, "E263.MirrorCS", {"start": v(26, -8) * mm, "end": v(21, -8) * mm});
            skLineSegment(sketch, "E264.MirrorCS", {"start": v(17, -17.4) * mm, "end": v(12, -17.4) * mm});
            skPoint(sketch, "E265.MirrorP", {"position": v(-14.5, -14.9) * mm});
            skLineSegment(sketch, "E266.MirrorCS", {"start": v(-21, -40.6) * mm, "end": v(-21, -45.6) * mm});
            skLineSegment(sketch, "E267.MirrorCS", {"start": v(8, -21.8) * mm, "end": v(3, -21.8) * mm});
            skLineSegment(sketch, "E268.MirrorCS", {"start": v(8, -36.2) * mm, "end": v(3, -36.2) * mm});
            skLineSegment(sketch, "E269.MirrorCS", {"start": v(30, -40.6) * mm, "end": v(30, -45.6) * mm});
            skPoint(sketch, "E270.MirrorP", {"position": v(14.5, -33.7) * mm});
            skLineSegment(sketch, "E271.MirrorCS", {"start": v(30, -31.2) * mm, "end": v(30, -36.2) * mm});
            skPoint(sketch, "E272.MirrorP", {"position": v(23.5, -33.7) * mm});
            skLineSegment(sketch, "E273.MirrorCS", {"start": v(17, -36.2) * mm, "end": v(12, -36.2) * mm});
            skLineSegment(sketch, "E274.MirrorCS", {"start": v(-35, -17.4) * mm, "end": v(-30, -17.4) * mm});
            skLineSegment(sketch, "E275.MirrorCS", {"start": v(-12, -12.4) * mm, "end": v(-12, -17.4) * mm});
            skLineSegment(sketch, "E276.MirrorCS", {"start": v(8, -50) * mm, "end": v(8, -55) * mm});
            skLineSegment(sketch, "E277.MirrorCS", {"start": v(35, -50) * mm, "end": v(30, -50) * mm});
            skLineSegment(sketch, "E278.MirrorCS", {"start": v(35, -55) * mm, "end": v(30, -55) * mm});
            skLineSegment(sketch, "E279.MirrorCS", {"start": v(17, -40.6) * mm, "end": v(17, -45.6) * mm});
            skLineSegment(sketch, "E280.MirrorCS", {"start": v(8, -12.4) * mm, "end": v(3, -12.4) * mm});
            skLineSegment(sketch, "E281.MirrorCS", {"start": v(-8, -40.6) * mm, "end": v(-8, -45.6) * mm});
            skLineSegment(sketch, "E282.MirrorCS", {"start": v(17, -8) * mm, "end": v(12, -8) * mm});
            skLineSegment(sketch, "E283.MirrorCS", {"start": v(-30, -50) * mm, "end": v(-30, -55) * mm});
            skPoint(sketch, "E284.MirrorP", {"position": v(-32.5, -33.7) * mm});
            skLineSegment(sketch, "E285.MirrorCS", {"start": v(-21, -3) * mm, "end": v(-21, -8) * mm});
            skLineSegment(sketch, "E286.MirrorCS", {"start": v(-26, -17.4) * mm, "end": v(-21, -17.4) * mm});
            skLineSegment(sketch, "E287.MirrorCS", {"start": v(-17, -55) * mm, "end": v(-12, -55) * mm});
            skLineSegment(sketch, "E288.MirrorCS", {"start": v(-21, -50) * mm, "end": v(-21, -55) * mm});
            skPoint(sketch, "E289.MirrorP", {"position": v(-23.5, -52.5) * mm});
            skLineSegment(sketch, "E290.MirrorCS", {"start": v(35, -21.8) * mm, "end": v(30, -21.8) * mm});
            skLineSegment(sketch, "E291.MirrorCS", {"start": v(-8, -21.8) * mm, "end": v(-3, -21.8) * mm});
            skLineSegment(sketch, "E292.MirrorCS", {"start": v(-17, -3) * mm, "end": v(-12, -3) * mm});
            skLineSegment(sketch, "E293.MirrorCS", {"start": v(-17, -12.4) * mm, "end": v(-12, -12.4) * mm});
            skLineSegment(sketch, "E294.MirrorCS", {"start": v(-26, -36.2) * mm, "end": v(-21, -36.2) * mm, "construction": true});
            skPoint(sketch, "E295.MirrorP", {"position": v(32.5, -33.7) * mm});
            skLineSegment(sketch, "E296.MirrorCS", {"start": v(35, -50) * mm, "end": v(35, -55) * mm});
            skLineSegment(sketch, "E297.MirrorCS", {"start": v(8, -26.8) * mm, "end": v(3, -26.8) * mm});
            skLineSegment(sketch, "E298.MirrorCS", {"start": v(35, -12.4) * mm, "end": v(30, -12.4) * mm});
            skLineSegment(sketch, "E299.MirrorCS", {"start": v(-12, -50) * mm, "end": v(-12, -55) * mm});
            skLineSegment(sketch, "E300.MirrorCS", {"start": v(-17, -8) * mm, "end": v(-12, -8) * mm});
            skLineSegment(sketch, "E301.MirrorCS", {"start": v(-26, -26.8) * mm, "end": v(-21, -26.8) * mm});
            skLineSegment(sketch, "E302.MirrorCS", {"start": v(30, -21.8) * mm, "end": v(30, -26.8) * mm});
            skLineSegment(sketch, "E303.MirrorCS", {"start": v(30, -50) * mm, "end": v(30, -55) * mm});
            skPoint(sketch, "E304.MirrorP", {"position": v(-5.5, -52.5) * mm});
            skPoint(sketch, "E305.MirrorP", {"position": v(-23.5, -14.9) * mm});
            skLineSegment(sketch, "E306.MirrorCS", {"start": v(17, -31.2) * mm, "end": v(17, -36.2) * mm});
            skPoint(sketch, "E307.MirrorP", {"position": v(-14.5, -33.7) * mm});
            skLineSegment(sketch, "E308.MirrorCS", {"start": v(8, -3) * mm, "end": v(3, -3) * mm, "construction": true});
            skLineSegment(sketch, "E309.MirrorCS", {"start": v(-8, -21.8) * mm, "end": v(-8, -26.8) * mm});
            skLineSegment(sketch, "E310.MirrorCS", {"start": v(-3, -3) * mm, "end": v(-3, -8) * mm, "construction": true});
            skLineSegment(sketch, "E311.MirrorCS", {"start": v(8, -17.4) * mm, "end": v(3, -17.4) * mm});
            skLineSegment(sketch, "E312.MirrorCS", {"start": v(-21, -31.2) * mm, "end": v(-21, -36.2) * mm, "construction": true});
            skLineSegment(sketch, "E313.MirrorCS", {"start": v(-17, -31.2) * mm, "end": v(-12, -31.2) * mm});
            skLineSegment(sketch, "E314.MirrorCS", {"start": v(35, -3) * mm, "end": v(30, -3) * mm});
            skLineSegment(sketch, "E315.MirrorCS", {"start": v(-35, -36.2) * mm, "end": v(-30, -36.2) * mm});
            skLineSegment(sketch, "E316.MirrorCS", {"start": v(-30, -21.8) * mm, "end": v(-30, -26.8) * mm});
            skLineSegment(sketch, "E317.MirrorCS", {"start": v(-30, -40.6) * mm, "end": v(-21, -40.6) * mm, "construction": true});
            skPoint(sketch, "E318.MirrorP", {"position": v(-32.5, -43.1) * mm});
            skLineSegment(sketch, "E319.MirrorCS", {"start": v(-17, -40.6) * mm, "end": v(-17, -45.6) * mm});
            skLineSegment(sketch, "E320.MirrorCS", {"start": v(-8, -12.4) * mm, "end": v(-8, -17.4) * mm});
            skLineSegment(sketch, "E321.MirrorCS", {"start": v(3, -50) * mm, "end": v(3, -40.6) * mm, "construction": true});
            skLineSegment(sketch, "E322.MirrorCS", {"start": v(21, -40.6) * mm, "end": v(21, -45.6) * mm});
            skLineSegment(sketch, "E323.MirrorCS", {"start": v(3, -31.2) * mm, "end": v(3, -36.2) * mm});
            skPoint(sketch, "E324.MirrorP", {"position": v(5.5, -24.3) * mm});
            skLineSegment(sketch, "E325.MirrorCS", {"start": v(30, -40.6) * mm, "end": v(21, -40.6) * mm, "construction": true});
            skPoint(sketch, "E326.MirrorP", {"position": v(-23.5, -33.7) * mm});
            skLineSegment(sketch, "E327.MirrorCS", {"start": v(26, -31.2) * mm, "end": v(26, -36.2) * mm, "construction": true});
            skPoint(sketch, "E328.MirrorP", {"position": v(-14.5, -5.5) * mm});
            skLineSegment(sketch, "E329.MirrorCS", {"start": v(3, -21.8) * mm, "end": v(3, -26.8) * mm});
            skLineSegment(sketch, "E330.MirrorCS", {"start": v(17, -12.4) * mm, "end": v(17, -17.4) * mm});
            skLineSegment(sketch, "E331.MirrorCS", {"start": v(-8, -50) * mm, "end": v(-3, -50) * mm});
            skLineSegment(sketch, "E332.MirrorCS", {"start": v(26, -55) * mm, "end": v(21, -55) * mm});
            skLineSegment(sketch, "E333.MirrorCS", {"start": v(26, -40.6) * mm, "end": v(26, -45.6) * mm});
            skLineSegment(sketch, "E334.MirrorCS", {"start": v(17, -21.8) * mm, "end": v(17, -26.8) * mm});
            skLineSegment(sketch, "E335.MirrorCS", {"start": v(30, -12.4) * mm, "end": v(30, -17.4) * mm});
            skLineSegment(sketch, "E336.MirrorCS", {"start": v(21, -31.2) * mm, "end": v(21, -36.2) * mm, "construction": true});
            skLineSegment(sketch, "E337.MirrorCS", {"start": v(-35, -55) * mm, "end": v(-30, -55) * mm});
            skLineSegment(sketch, "E338.MirrorCS", {"start": v(-30, -3) * mm, "end": v(-30, -8) * mm});
            skLineSegment(sketch, "E339.MirrorCS", {"start": v(-35, -40.6) * mm, "end": v(-35, -45.6) * mm});
            skLineSegment(sketch, "E340.MirrorCS", {"start": v(-35, -21.8) * mm, "end": v(-35, -26.8) * mm});
            skPoint(sketch, "E341.MirrorP", {"position": v(14.5, -24.3) * mm});
            skLineSegment(sketch, "E342.MirrorCS", {"start": v(30, -3) * mm, "end": v(30, -8) * mm});
            skLineSegment(sketch, "E343.MirrorCS", {"start": v(-26, -50) * mm, "end": v(-26, -55) * mm});
            skLineSegment(sketch, "E344.MirrorCS", {"start": v(-26, -8) * mm, "end": v(-21, -8) * mm});
            skPoint(sketch, "E345.MirrorP", {"position": v(23.5, -24.3) * mm});
            skPoint(sketch, "E346.MirrorP", {"position": v(-32.5, -5.5) * mm});
            skPoint(sketch, "E347.MirrorP", {"position": v(-32.5, -14.9) * mm});
            skLineSegment(sketch, "E348.MirrorCS", {"start": v(-3, -31.2) * mm, "end": v(-3, -36.2) * mm});
            skLineSegment(sketch, "E349.MirrorCS", {"start": v(8, -8) * mm, "end": v(3, -8) * mm, "construction": true});
            skLineSegment(sketch, "E350.MirrorCS", {"start": v(-35, -40.6) * mm, "end": v(-30, -40.6) * mm});
            skLineSegment(sketch, "E351.MirrorCS", {"start": v(-35, -3) * mm, "end": v(-30, -3) * mm});
            skLineSegment(sketch, "E352.MirrorCS", {"start": v(-8, -12.4) * mm, "end": v(-3, -12.4) * mm});
            skLineSegment(sketch, "E353.MirrorCS", {"start": v(-35, -50) * mm, "end": v(-35, -55) * mm});
            skLineSegment(sketch, "E354.MirrorCS", {"start": v(21, -21.8) * mm, "end": v(21, -26.8) * mm});
            skLineSegment(sketch, "E355.MirrorCS", {"start": v(3, -12.4) * mm, "end": v(3, -17.4) * mm});
            skLineSegment(sketch, "E356.MirrorCS", {"start": v(17, -3) * mm, "end": v(17, -8) * mm});
            skLineSegment(sketch, "E357.MirrorCS", {"start": v(-17, -12.4) * mm, "end": v(-17, -17.4) * mm});
            skLineSegment(sketch, "E358.MirrorCS", {"start": v(21, -50) * mm, "end": v(21, -55) * mm});
            skPoint(sketch, "E359.MirrorP", {"position": v(-14.5, -43.1) * mm});
            skPoint(sketch, "E360.MirrorP", {"position": v(-5.5, -33.7) * mm});
            skLineSegment(sketch, "E361.MirrorCS", {"start": v(30, -50) * mm, "end": v(21, -50) * mm, "construction": true});
            skLineSegment(sketch, "E362.MirrorCS", {"start": v(-30, -12.4) * mm, "end": v(-21, -12.4) * mm, "construction": true});
            skLineSegment(sketch, "E363.MirrorCS", {"start": v(-26, -21.8) * mm, "end": v(-26, -26.8) * mm});
            skPoint(sketch, "E364.MirrorP", {"position": v(32.5, -52.5) * mm});
            skLineSegment(sketch, "E365.MirrorCS", {"start": v(35, -36.2) * mm, "end": v(30, -36.2) * mm});
            skLineSegment(sketch, "E366.MirrorCS", {"start": v(-35, -3) * mm, "end": v(-35, -8) * mm});
            skLineSegment(sketch, "E367.MirrorCS", {"start": v(-30, -31.2) * mm, "end": v(-30, -36.2) * mm});
            skLineSegment(sketch, "E368.MirrorCS", {"start": v(-30, -40.6) * mm, "end": v(-30, -45.6) * mm});
            skLineSegment(sketch, "E369.MirrorCS", {"start": v(-26, -55) * mm, "end": v(-21, -55) * mm});
            skLineSegment(sketch, "E370.MirrorCS", {"start": v(-8, -36.2) * mm, "end": v(-3, -36.2) * mm});
            skLineSegment(sketch, "E371.MirrorCS", {"start": v(-8, -31.2) * mm, "end": v(-3, -31.2) * mm});
            skPoint(sketch, "E372.MirrorP", {"position": v(32.5, -24.3) * mm});
            skLineSegment(sketch, "E373.MirrorCS", {"start": v(-35, -21.8) * mm, "end": v(-30, -21.8) * mm});
            skLineSegment(sketch, "E374.MirrorCS", {"start": v(-26, -40.6) * mm, "end": v(-26, -45.6) * mm});
            skLineSegment(sketch, "E375.MirrorCS", {"start": v(-8, -8) * mm, "end": v(-3, -8) * mm, "construction": true});
            skLineSegment(sketch, "E376.MirrorCS", {"start": v(17, -45.6) * mm, "end": v(12, -45.6) * mm});
            skPoint(sketch, "E377.MirrorP", {"position": v(23.5, -43.1) * mm});
            skLineSegment(sketch, "E378.MirrorCS", {"start": v(26, -50) * mm, "end": v(26, -55) * mm});
            skLineSegment(sketch, "E379.MirrorCS", {"start": v(-12, -21.8) * mm, "end": v(-12, -26.8) * mm});
            skLineSegment(sketch, "E380.MirrorCS", {"start": v(-17, -31.2) * mm, "end": v(-17, -36.2) * mm});
            skLineSegment(sketch, "E381.MirrorCS", {"start": v(21, -12.4) * mm, "end": v(21, -17.4) * mm});
            skLineSegment(sketch, "E382.MirrorCS", {"start": v(17, -50) * mm, "end": v(17, -55) * mm});
            skLineSegment(sketch, "E383.MirrorCS", {"start": v(26, -45.6) * mm, "end": v(21, -45.6) * mm});
            skPoint(sketch, "E384.MirrorP", {"position": v(5.5, -43.1) * mm});
            skLineSegment(sketch, "E385.MirrorCS", {"start": v(8, -31.2) * mm, "end": v(8, -36.2) * mm});
            skLineSegment(sketch, "E386.MirrorCS", {"start": v(12, -21.8) * mm, "end": v(12, -26.8) * mm});
            skLineSegment(sketch, "E387.MirrorCS", {"start": v(-12, -40.6) * mm, "end": v(-12, -45.6) * mm});
            skLineSegment(sketch, "E388.MirrorCS", {"start": v(35, -26.8) * mm, "end": v(30, -26.8) * mm});
            skLineSegment(sketch, "E389.MirrorCS", {"start": v(-3, -21.8) * mm, "end": v(-3, -26.8) * mm});
            skLineSegment(sketch, "E390.MirrorCS", {"start": v(-17, -40.6) * mm, "end": v(-12, -40.6) * mm});
            skLineSegment(sketch, "E391.MirrorCS", {"start": v(-35, -26.8) * mm, "end": v(-30, -26.8) * mm});
            skLineSegment(sketch, "E392.MirrorCS", {"start": v(-35, -50) * mm, "end": v(-30, -50) * mm});
            skLineSegment(sketch, "E393.MirrorCS", {"start": v(21, -3) * mm, "end": v(21, -8) * mm});
            skLineSegment(sketch, "E394.MirrorCS", {"start": v(12, -31.2) * mm, "end": v(12, -36.2) * mm});
            skLineSegment(sketch, "E395.MirrorCS", {"start": v(-8, -55) * mm, "end": v(-3, -55) * mm});
            skLineSegment(sketch, "E396.MirrorCS", {"start": v(-17, -21.8) * mm, "end": v(-17, -26.8) * mm});
            skPoint(sketch, "E397.MirrorP", {"position": v(5.5, -14.9) * mm});
            skPoint(sketch, "E398.MirrorP", {"position": v(5.5, -5.5) * mm});
            skLineSegment(sketch, "E399.MirrorCS", {"start": v(-3, -12.4) * mm, "end": v(-3, -17.4) * mm});
            skPoint(sketch, "E400.MirrorP", {"position": v(-32.5, -24.3) * mm});
            skLineSegment(sketch, "E401.MirrorCS", {"start": v(35, -3) * mm, "end": v(35, -8) * mm});
            skLineSegment(sketch, "E402.MirrorCS", {"start": v(35, -40.6) * mm, "end": v(35, -45.6) * mm});
            skLineSegment(sketch, "E403.MirrorCS", {"start": v(-35, -12.4) * mm, "end": v(-30, -12.4) * mm});
            skLineSegment(sketch, "E404.MirrorCS", {"start": v(35, -31.2) * mm, "end": v(35, -36.2) * mm});
            skLineSegment(sketch, "E405.MirrorCS", {"start": v(-26, -45.6) * mm, "end": v(-21, -45.6) * mm});
            skPoint(sketch, "E406.MirrorP", {"position": v(14.5, -52.5) * mm});
            skPoint(sketch, "E407.MirrorP", {"position": v(23.5, -52.5) * mm});
            skLineSegment(sketch, "E408.MirrorCS", {"start": v(3, -3) * mm, "end": v(3, -8) * mm, "construction": true});
            skLineSegment(sketch, "E409.MirrorCS", {"start": v(-17, -3) * mm, "end": v(-17, -8) * mm});
            skLineSegment(sketch, "E410.MirrorCS", {"start": v(35, -12.4) * mm, "end": v(35, -17.4) * mm});
            skLineSegment(sketch, "E411.MirrorCS", {"start": v(12, -12.4) * mm, "end": v(12, -17.4) * mm});
            skLineSegment(sketch, "E412.MirrorCS", {"start": v(-17, -50) * mm, "end": v(-12, -50) * mm});
            skPoint(sketch, "E413.MirrorP", {"position": v(14.5, -14.9) * mm});
            skLineSegment(sketch, "E414.MirrorCS", {"start": v(35, -8) * mm, "end": v(30, -8) * mm});
            skLineSegment(sketch, "E415.MirrorCS", {"start": v(-8, -45.6) * mm, "end": v(-3, -45.6) * mm});
            skPoint(sketch, "E416.MirrorP", {"position": v(-14.5, -24.3) * mm});
            skLineSegment(sketch, "E417.MirrorCS", {"start": v(12, -40.6) * mm, "end": v(12, -45.6) * mm});
            skLineSegment(sketch, "E418.MirrorCS", {"start": v(-30, -12.4) * mm, "end": v(-30, -17.4) * mm});
            skLineSegment(sketch, "E419.MirrorCS", {"start": v(-26, -3) * mm, "end": v(-26, -8) * mm});
            skLineSegment(sketch, "E420.MirrorCS", {"start": v(-35, -8) * mm, "end": v(-30, -8) * mm});
            skSolve(sketch);
        }
        {
            var Q0;
            Q0 = qSketchRegion(id + "F0", true);
            extrude(context, id + "F1", {"entities" : qUnion([Q0]), "depth" : 3 * mm, "offsetDistance" : 25 * mm});
        }
        {
            var Q0;
            Q0=qCreatedBy(makeId("Top.planeOp"),FACE);
            var sketch = newSketch(context, id + "F2", { "sketchPlane" : qUnion([Q0])});
            skLineSegment(sketch, "E421.rect.bottom", {"start": v(28, -57.05) * mm, "end": v(28, 27.95) * mm});
            skLineSegment(sketch, "E421.rect.top", {"start": v(-28, -57.05) * mm, "end": v(-28, 27.95) * mm});
            skLineSegment(sketch, "E421.rect.left", {"start": v(28, -57.05) * mm, "end": v(-28, -57.05) * mm});
            skLineSegment(sketch, "E421.rect.right", {"start": v(28, 27.95) * mm, "end": v(-28, 27.95) * mm});
            skPoint(sketch, "E421.rect.middle", {"position": v(0, -14.55) * mm});
            skLineSegment(sketch, "E422.rect.bottom", {"start": v(24.5, -33.55) * mm, "end": v(24.5, 24.45) * mm, "construction": true});
            skLineSegment(sketch, "E422.rect.top", {"start": v(-24.5, -33.55) * mm, "end": v(-24.5, 24.45) * mm, "construction": true});
            skLineSegment(sketch, "E422.rect.left", {"start": v(24.5, -33.55) * mm, "end": v(-24.5, -33.55) * mm, "construction": true});
            skLineSegment(sketch, "E422.rect.right", {"start": v(24.5, 24.45) * mm, "end": v(-24.5, 24.45) * mm, "construction": true});
            skPoint(sketch, "E422.rect.middle", {"position": v(0, -4.55) * mm});
            skCircle(sketch, "E423", {"center": v(-24.5, -33.55) * mm, "radius": 1.38 * mm});
            skCircle(sketch, "E424", {"center": v(-24.5, 24.45) * mm, "radius": 1.38 * mm});
            skCircle(sketch, "E425", {"center": v(24.5, 24.45) * mm, "radius": 1.38 * mm});
            skCircle(sketch, "E426", {"center": v(24.5, -33.55) * mm, "radius": 1.38 * mm});
            skSolve(sketch);
        }
        {
            var Q0;
            Q0=makeQuery(id+"F1.opExtrude","CAP_FACE",FACE,{"disambiguationData":[OSD([sQuery(id+"F0.wireOp",EDGE,"E2"),sQuery(id+"F0.wireOp",EDGE,"E3"),sQuery(id+"F0.wireOp",EDGE,"E4"),sQuery(id+"F0.wireOp",EDGE,"E5"),sQuery(id+"F0.wireOp",EDGE,"E6.MirrorCS"),sQuery(id+"F0.wireOp",EDGE,"E7.MirrorCS"),sQuery(id+"F0.wireOp",EDGE,"E8.MirrorCS"),sQuery(id+"F0.wireOp",EDGE,"E9.MirrorCS"),sQuery(id+"F0.wireOp",EDGE,"E10.MirrorCS"),sQuery(id+"F0.wireOp",EDGE,"E11"),sQuery(id+"F0.wireOp",EDGE,"E12"),sQuery(id+"F0.wireOp",EDGE,"E14.MirrorC"),sQuery(id+"F0.wireOp",EDGE,"E15.MirrorC"),sQuery(id+"F0.wireOp",EDGE,"E16"),sQuery(id+"F0.wireOp",EDGE,"E17"),sQuery(id+"F0.wireOp",EDGE,"E18.MirrorCS"),sQuery(id+"F0.wireOp",EDGE,"E19.MirrorCS"),sQuery(id+"F0.wireOp",EDGE,"E20.MirrorCS"),sQuery(id+"F0.wireOp",EDGE,"E21.MirrorCS"),sQuery(id+"F0.wireOp",EDGE,"E22.MirrorCS"),sQuery(id+"F0.wireOp",EDGE,"E23.MirrorCS"),sQuery(id+"F0.wireOp",EDGE,"E24.MirrorCS"),sQuery(id+"F0.wireOp",EDGE,"E25.MirrorCS"),sQuery(id+"F0.wireOp",EDGE,"E26.MirrorCS"),sQuery(id+"F0.wireOp",EDGE,"E27.MirrorCS"),sQuery(id+"F0.wireOp",EDGE,"E28.MirrorCS"),sQuery(id+"F0.wireOp",EDGE,"E29.MirrorCS"),sQuery(id+"F0.wireOp",EDGE,"E30.MirrorCS"),sQuery(id+"F0.wireOp",EDGE,"E31.MirrorC"),sQuery(id+"F0.wireOp",EDGE,"E32.MirrorC"),sQuery(id+"F0.wireOp",EDGE,"E33.MirrorC"),sQuery(id+"F0.wireOp",EDGE,"E34.MirrorC"),sQuery(id+"F0.wireOp",EDGE,"5c3mzxsr-oUSN-SXrm-x3ZU-d6UrBw8qLIhU.bottom"),sQuery(id+"F0.wireOp",EDGE,"5c3mzxsr-oUSN-SXrm-x3ZU-d6UrBw8qLIhU.top"),sQuery(id+"F0.wireOp",EDGE,"5c3mzxsr-oUSN-SXrm-x3ZU-d6UrBw8qLIhU.left"),sQuery(id+"F0.wireOp",EDGE,"5c3mzxsr-oUSN-SXrm-x3ZU-d6UrBw8qLIhU.right"),sQuery(id+"F0.wireOp",EDGE,"544fddae-270f-44da-af1d-2d8b63806ee7.1.0.0"),sQuery(id+"F0.wireOp",EDGE,"544fddae-270f-44da-af1d-2d8b63806ee7.1.0.1"),sQuery(id+"F0.wireOp",EDGE,"544fddae-270f-44da-af1d-2d8b63806ee7.1.0.2"),sQuery(id+"F0.wireOp",EDGE,"544fddae-270f-44da-af1d-2d8b63806ee7.1.0.3"),sQuery(id+"F0.wireOp",EDGE,"544fddae-270f-44da-af1d-2d8b63806ee7.2.0.0"),sQuery(id+"F0.wireOp",EDGE,"544fddae-270f-44da-af1d-2d8b63806ee7.2.0.1"),sQuery(id+"F0.wireOp",EDGE,"544fddae-270f-44da-af1d-2d8b63806ee7.2.0.2"),sQuery(id+"F0.wireOp",EDGE,"544fddae-270f-44da-af1d-2d8b63806ee7.2.0.3"),sQuery(id+"F0.wireOp",EDGE,"e76ad390-1c26-47f0-865e-979589794fca.0.3.0"),sQuery(id+"F0.wireOp",EDGE,"e76ad390-1c26-47f0-865e-979589794fca.3.3.0"),sQuery(id+"F0.wireOp",EDGE,"e76ad390-1c26-47f0-865e-979589794fca.6.3.0"),sQuery(id+"F0.wireOp",EDGE,"e76ad390-1c26-47f0-865e-979589794fca.9.3.0"),sQuery(id+"F0.wireOp",EDGE,"f5af7e2b-df8b-4b93-8138-36ea322a7ab3.1.0.0"),sQuery(id+"F0.wireOp",EDGE,"f5af7e2b-df8b-4b93-8138-36ea322a7ab3.1.0.1"),sQuery(id+"F0.wireOp",EDGE,"f5af7e2b-df8b-4b93-8138-36ea322a7ab3.1.0.2"),sQuery(id+"F0.wireOp",EDGE,"f5af7e2b-df8b-4b93-8138-36ea322a7ab3.1.0.3"),sQuery(id+"F0.wireOp",EDGE,"f5af7e2b-df8b-4b93-8138-36ea322a7ab3.1.0.4"),sQuery(id+"F0.wireOp",EDGE,"f5af7e2b-df8b-4b93-8138-36ea322a7ab3.1.0.5"),sQuery(id+"F0.wireOp",EDGE,"f5af7e2b-df8b-4b93-8138-36ea322a7ab3.1.0.6"),sQuery(id+"F0.wireOp",EDGE,"f5af7e2b-df8b-4b93-8138-36ea322a7ab3.1.0.7"),sQuery(id+"F0.wireOp",EDGE,"f5af7e2b-df8b-4b93-8138-36ea322a7ab3.1.0.8"),sQuery(id+"F0.wireOp",EDGE,"f5af7e2b-df8b-4b93-8138-36ea322a7ab3.1.0.9"),sQuery(id+"F0.wireOp",EDGE,"f5af7e2b-df8b-4b93-8138-36ea322a7ab3.1.0.10"),sQuery(id+"F0.wireOp",EDGE,"f5af7e2b-df8b-4b93-8138-36ea322a7ab3.1.0.11"),sQuery(id+"F0.wireOp",EDGE,"f5af7e2b-df8b-4b93-8138-36ea322a7ab3.1.0.12"),sQuery(id+"F0.wireOp",EDGE,"f5af7e2b-df8b-4b93-8138-36ea322a7ab3.1.0.13"),sQuery(id+"F0.wireOp",EDGE,"f5af7e2b-df8b-4b93-8138-36ea322a7ab3.1.0.14"),sQuery(id+"F0.wireOp",EDGE,"f5af7e2b-df8b-4b93-8138-36ea322a7ab3.1.0.15"),sQuery(id+"F0.wireOp",EDGE,"f5af7e2b-df8b-4b93-8138-36ea322a7ab3.2.0.0"),sQuery(id+"F0.wireOp",EDGE,"f5af7e2b-df8b-4b93-8138-36ea322a7ab3.2.0.1"),sQuery(id+"F0.wireOp",EDGE,"f5af7e2b-df8b-4b93-8138-36ea322a7ab3.2.0.2"),sQuery(id+"F0.wireOp",EDGE,"f5af7e2b-df8b-4b93-8138-36ea322a7ab3.2.0.3"),sQuery(id+"F0.wireOp",EDGE,"f5af7e2b-df8b-4b93-8138-36ea322a7ab3.2.0.4"),sQuery(id+"F0.wireOp",EDGE,"f5af7e2b-df8b-4b93-8138-36ea322a7ab3.2.0.5"),sQuery(id+"F0.wireOp",EDGE,"f5af7e2b-df8b-4b93-8138-36ea322a7ab3.2.0.6"),sQuery(id+"F0.wireOp",EDGE,"f5af7e2b-df8b-4b93-8138-36ea322a7ab3.2.0.7"),sQuery(id+"F0.wireOp",EDGE,"f5af7e2b-df8b-4b93-8138-36ea322a7ab3.2.0.8"),sQuery(id+"F0.wireOp",EDGE,"f5af7e2b-df8b-4b93-8138-36ea322a7ab3.2.0.9"),sQuery(id+"F0.wireOp",EDGE,"f5af7e2b-df8b-4b93-8138-36ea322a7ab3.2.0.10"),sQuery(id+"F0.wireOp",EDGE,"f5af7e2b-df8b-4b93-8138-36ea322a7ab3.2.0.11"),sQuery(id+"F0.wireOp",EDGE,"f5af7e2b-df8b-4b93-8138-36ea322a7ab3.2.0.12"),sQuery(id+"F0.wireOp",EDGE,"f5af7e2b-df8b-4b93-8138-36ea322a7ab3.2.0.13"),sQuery(id+"F0.wireOp",EDGE,"f5af7e2b-df8b-4b93-8138-36ea322a7ab3.2.0.14"),sQuery(id+"F0.wireOp",EDGE,"f5af7e2b-df8b-4b93-8138-36ea322a7ab3.2.0.15"),sQuery(id+"F0.wireOp",EDGE,"f5af7e2b-df8b-4b93-8138-36ea322a7ab3.3.0.0"),sQuery(id+"F0.wireOp",EDGE,"f5af7e2b-df8b-4b93-8138-36ea322a7ab3.3.0.1"),sQuery(id+"F0.wireOp",EDGE,"f5af7e2b-df8b-4b93-8138-36ea322a7ab3.3.0.2"),sQuery(id+"F0.wireOp",EDGE,"f5af7e2b-df8b-4b93-8138-36ea322a7ab3.3.0.3"),sQuery(id+"F0.wireOp",EDGE,"f5af7e2b-df8b-4b93-8138-36ea322a7ab3.3.0.5"),sQuery(id+"F0.wireOp",EDGE,"f5af7e2b-df8b-4b93-8138-36ea322a7ab3.3.0.6"),sQuery(id+"F0.wireOp",EDGE,"f5af7e2b-df8b-4b93-8138-36ea322a7ab3.3.0.7"),sQuery(id+"F0.wireOp",EDGE,"f5af7e2b-df8b-4b93-8138-36ea322a7ab3.3.0.8"),sQuery(id+"F0.wireOp",EDGE,"f5af7e2b-df8b-4b93-8138-36ea322a7ab3.3.0.10"),sQuery(id+"F0.wireOp",EDGE,"f5af7e2b-df8b-4b93-8138-36ea322a7ab3.3.0.11"),sQuery(id+"F0.wireOp",EDGE,"f5af7e2b-df8b-4b93-8138-36ea322a7ab3.3.0.13"),sQuery(id+"F0.wireOp",EDGE,"f5af7e2b-df8b-4b93-8138-36ea322a7ab3.3.0.14"),sQuery(id+"F0.wireOp",EDGE,"f5af7e2b-df8b-4b93-8138-36ea322a7ab3.4.0.0"),sQuery(id+"F0.wireOp",EDGE,"f5af7e2b-df8b-4b93-8138-36ea322a7ab3.4.0.1"),sQuery(id+"F0.wireOp",EDGE,"f5af7e2b-df8b-4b93-8138-36ea322a7ab3.4.0.2"),sQuery(id+"F0.wireOp",EDGE,"f5af7e2b-df8b-4b93-8138-36ea322a7ab3.4.0.3"),sQuery(id+"F0.wireOp",EDGE,"f5af7e2b-df8b-4b93-8138-36ea322a7ab3.4.0.4"),sQuery(id+"F0.wireOp",EDGE,"f5af7e2b-df8b-4b93-8138-36ea322a7ab3.4.0.5"),sQuery(id+"F0.wireOp",EDGE,"f5af7e2b-df8b-4b93-8138-36ea322a7ab3.4.0.6"),sQuery(id+"F0.wireOp",EDGE,"f5af7e2b-df8b-4b93-8138-36ea322a7ab3.4.0.7"),sQuery(id+"F0.wireOp",EDGE,"f5af7e2b-df8b-4b93-8138-36ea322a7ab3.4.0.8"),sQuery(id+"F0.wireOp",EDGE,"f5af7e2b-df8b-4b93-8138-36ea322a7ab3.4.0.9"),sQuery(id+"F0.wireOp",EDGE,"f5af7e2b-df8b-4b93-8138-36ea322a7ab3.4.0.10"),sQuery(id+"F0.wireOp",EDGE,"f5af7e2b-df8b-4b93-8138-36ea322a7ab3.4.0.11"),sQuery(id+"F0.wireOp",EDGE,"f5af7e2b-df8b-4b93-8138-36ea322a7ab3.4.0.12"),sQuery(id+"F0.wireOp",EDGE,"f5af7e2b-df8b-4b93-8138-36ea322a7ab3.4.0.13"),sQuery(id+"F0.wireOp",EDGE,"f5af7e2b-df8b-4b93-8138-36ea322a7ab3.4.0.14"),sQuery(id+"F0.wireOp",EDGE,"f5af7e2b-df8b-4b93-8138-36ea322a7ab3.4.0.15"),sQuery(id+"F0.wireOp",EDGE,"2337b784-ced5-4511-8511-f3861e9e9c320.MirrorCS"),sQuery(id+"F0.wireOp",EDGE,"2337b784-ced5-4511-8511-f3861e9e9c321.MirrorCS"),sQuery(id+"F0.wireOp",EDGE,"2337b784-ced5-4511-8511-f3861e9e9c322.MirrorCS"),sQuery(id+"F0.wireOp",EDGE,"2337b784-ced5-4511-8511-f3861e9e9c323.MirrorCS"),sQuery(id+"F0.wireOp",EDGE,"2337b784-ced5-4511-8511-f3861e9e9c324.MirrorCS"),sQuery(id+"F0.wireOp",EDGE,"2337b784-ced5-4511-8511-f3861e9e9c325.MirrorCS"),sQuery(id+"F0.wireOp",EDGE,"2337b784-ced5-4511-8511-f3861e9e9c326.MirrorCS"),sQuery(id+"F0.wireOp",EDGE,"2337b784-ced5-4511-8511-f3861e9e9c327.MirrorCS"),sQuery(id+"F0.wireOp",EDGE,"2337b784-ced5-4511-8511-f3861e9e9c328.MirrorCS"),sQuery(id+"F0.wireOp",EDGE,"2337b784-ced5-4511-8511-f3861e9e9c329.MirrorCS"),sQuery(id+"F0.wireOp",EDGE,"2337b784-ced5-4511-8511-f3861e9e9c3210.MirrorCS"),sQuery(id+"F0.wireOp",EDGE,"2337b784-ced5-4511-8511-f3861e9e9c3211.MirrorCS"),sQuery(id+"F0.wireOp",EDGE,"2337b784-ced5-4511-8511-f3861e9e9c3212.MirrorCS"),sQuery(id+"F0.wireOp",EDGE,"2337b784-ced5-4511-8511-f3861e9e9c3214.MirrorCS"),sQuery(id+"F0.wireOp",EDGE,"2337b784-ced5-4511-8511-f3861e9e9c3215.MirrorCS"),sQuery(id+"F0.wireOp",EDGE,"2337b784-ced5-4511-8511-f3861e9e9c3216.MirrorCS"),sQuery(id+"F0.wireOp",EDGE,"2337b784-ced5-4511-8511-f3861e9e9c3217.MirrorCS"),sQuery(id+"F0.wireOp",EDGE,"2337b784-ced5-4511-8511-f3861e9e9c3218.MirrorCS"),sQuery(id+"F0.wireOp",EDGE,"2337b784-ced5-4511-8511-f3861e9e9c3219.MirrorCS"),sQuery(id+"F0.wireOp",EDGE,"2337b784-ced5-4511-8511-f3861e9e9c3220.MirrorCS"),sQuery(id+"F0.wireOp",EDGE,"2337b784-ced5-4511-8511-f3861e9e9c3221.MirrorCS"),sQuery(id+"F0.wireOp",EDGE,"2337b784-ced5-4511-8511-f3861e9e9c3222.MirrorCS"),sQuery(id+"F0.wireOp",EDGE,"2337b784-ced5-4511-8511-f3861e9e9c3223.MirrorCS"),sQuery(id+"F0.wireOp",EDGE,"2337b784-ced5-4511-8511-f3861e9e9c3224.MirrorCS"),sQuery(id+"F0.wireOp",EDGE,"2337b784-ced5-4511-8511-f3861e9e9c3225.MirrorCS"),sQuery(id+"F0.wireOp",EDGE,"2337b784-ced5-4511-8511-f3861e9e9c3229.MirrorCS"),sQuery(id+"F0.wireOp",EDGE,"2337b784-ced5-4511-8511-f3861e9e9c3230.MirrorCS"),sQuery(id+"F0.wireOp",EDGE,"2337b784-ced5-4511-8511-f3861e9e9c3231.MirrorCS"),sQuery(id+"F0.wireOp",EDGE,"2337b784-ced5-4511-8511-f3861e9e9c3232.MirrorCS"),sQuery(id+"F0.wireOp",EDGE,"2337b784-ced5-4511-8511-f3861e9e9c3233.MirrorCS"),sQuery(id+"F0.wireOp",EDGE,"2337b784-ced5-4511-8511-f3861e9e9c3234.MirrorCS"),sQuery(id+"F0.wireOp",EDGE,"2337b784-ced5-4511-8511-f3861e9e9c3235.MirrorCS"),sQuery(id+"F0.wireOp",EDGE,"2337b784-ced5-4511-8511-f3861e9e9c3236.MirrorCS"),sQuery(id+"F0.wireOp",EDGE,"2337b784-ced5-4511-8511-f3861e9e9c3237.MirrorCS"),sQuery(id+"F0.wireOp",EDGE,"2337b784-ced5-4511-8511-f3861e9e9c3238.MirrorCS"),sQuery(id+"F0.wireOp",EDGE,"2337b784-ced5-4511-8511-f3861e9e9c3239.MirrorCS"),sQuery(id+"F0.wireOp",EDGE,"2337b784-ced5-4511-8511-f3861e9e9c3240.MirrorCS"),sQuery(id+"F0.wireOp",EDGE,"2337b784-ced5-4511-8511-f3861e9e9c3241.MirrorCS"),sQuery(id+"F0.wireOp",EDGE,"2337b784-ced5-4511-8511-f3861e9e9c3242.MirrorCS"),sQuery(id+"F0.wireOp",EDGE,"2337b784-ced5-4511-8511-f3861e9e9c3243.MirrorCS"),sQuery(id+"F0.wireOp",EDGE,"2337b784-ced5-4511-8511-f3861e9e9c3244.MirrorCS"),sQuery(id+"F0.wireOp",EDGE,"2337b784-ced5-4511-8511-f3861e9e9c3245.MirrorCS"),sQuery(id+"F0.wireOp",EDGE,"2337b784-ced5-4511-8511-f3861e9e9c3246.MirrorCS"),sQuery(id+"F0.wireOp",EDGE,"2337b784-ced5-4511-8511-f3861e9e9c3247.MirrorCS"),sQuery(id+"F0.wireOp",EDGE,"2337b784-ced5-4511-8511-f3861e9e9c3248.MirrorCS"),sQuery(id+"F0.wireOp",EDGE,"2337b784-ced5-4511-8511-f3861e9e9c3249.MirrorCS"),sQuery(id+"F0.wireOp",EDGE,"2337b784-ced5-4511-8511-f3861e9e9c3250.MirrorCS"),sQuery(id+"F0.wireOp",EDGE,"2337b784-ced5-4511-8511-f3861e9e9c3251.MirrorCS"),sQuery(id+"F0.wireOp",EDGE,"2337b784-ced5-4511-8511-f3861e9e9c3252.MirrorCS"),sQuery(id+"F0.wireOp",EDGE,"2337b784-ced5-4511-8511-f3861e9e9c3253.MirrorCS"),sQuery(id+"F0.wireOp",EDGE,"2337b784-ced5-4511-8511-f3861e9e9c3254.MirrorCS"),sQuery(id+"F0.wireOp",EDGE,"2337b784-ced5-4511-8511-f3861e9e9c3255.MirrorCS"),sQuery(id+"F0.wireOp",EDGE,"2337b784-ced5-4511-8511-f3861e9e9c3256.MirrorCS"),sQuery(id+"F0.wireOp",EDGE,"2337b784-ced5-4511-8511-f3861e9e9c3257.MirrorCS"),sQuery(id+"F0.wireOp",EDGE,"2337b784-ced5-4511-8511-f3861e9e9c3258.MirrorCS"),sQuery(id+"F0.wireOp",EDGE,"2337b784-ced5-4511-8511-f3861e9e9c3259.MirrorCS"),sQuery(id+"F0.wireOp",EDGE,"2337b784-ced5-4511-8511-f3861e9e9c3260.MirrorCS"),sQuery(id+"F0.wireOp",EDGE,"2337b784-ced5-4511-8511-f3861e9e9c3261.MirrorCS"),sQuery(id+"F0.wireOp",EDGE,"2337b784-ced5-4511-8511-f3861e9e9c3262.MirrorCS"),sQuery(id+"F0.wireOp",EDGE,"2337b784-ced5-4511-8511-f3861e9e9c3263.MirrorCS"),sQuery(id+"F0.wireOp",EDGE,"2337b784-ced5-4511-8511-f3861e9e9c3264.MirrorCS"),sQuery(id+"F0.wireOp",EDGE,"2337b784-ced5-4511-8511-f3861e9e9c3265.MirrorCS"),sQuery(id+"F0.wireOp",EDGE,"2337b784-ced5-4511-8511-f3861e9e9c3267.MirrorCS"),sQuery(id+"F0.wireOp",EDGE,"2337b784-ced5-4511-8511-f3861e9e9c3268.MirrorCS"),sQuery(id+"F0.wireOp",EDGE,"2337b784-ced5-4511-8511-f3861e9e9c3269.MirrorCS"),sQuery(id+"F0.wireOp",EDGE,"2337b784-ced5-4511-8511-f3861e9e9c3270.MirrorCS"),sQuery(id+"F0.wireOp",EDGE,"2337b784-ced5-4511-8511-f3861e9e9c3271.MirrorCS"),sQuery(id+"F0.wireOp",EDGE,"2337b784-ced5-4511-8511-f3861e9e9c3273.MirrorCS"),sQuery(id+"F0.wireOp",EDGE,"2337b784-ced5-4511-8511-f3861e9e9c3274.MirrorCS"),sQuery(id+"F0.wireOp",EDGE,"2337b784-ced5-4511-8511-f3861e9e9c3275.MirrorCS"),sQuery(id+"F0.wireOp",EDGE,"2337b784-ced5-4511-8511-f3861e9e9c3276.MirrorCS"),sQuery(id+"F0.wireOp",EDGE,"2337b784-ced5-4511-8511-f3861e9e9c3277.MirrorCS"),sQuery(id+"F0.wireOp",EDGE,"2337b784-ced5-4511-8511-f3861e9e9c3278.MirrorCS"),sQuery(id+"F0.wireOp",EDGE,"2337b784-ced5-4511-8511-f3861e9e9c3279.MirrorCS"),sQuery(id+"F0.wireOp",EDGE,"2337b784-ced5-4511-8511-f3861e9e9c3280.MirrorCS"),sQuery(id+"F0.wireOp",EDGE,"2337b784-ced5-4511-8511-f3861e9e9c3281.MirrorCS"),sQuery(id+"F0.wireOp",EDGE,"fa991f73-764b-433c-8341-ae9763ec17560.MirrorCS"),sQuery(id+"F0.wireOp",EDGE,"fa991f73-764b-433c-8341-ae9763ec17563.MirrorCS"),sQuery(id+"F0.wireOp",EDGE,"fa991f73-764b-433c-8341-ae9763ec17564.MirrorCS"),sQuery(id+"F0.wireOp",EDGE,"fa991f73-764b-433c-8341-ae9763ec17565.MirrorCS"),sQuery(id+"F0.wireOp",EDGE,"fa991f73-764b-433c-8341-ae9763ec17566.MirrorCS"),sQuery(id+"F0.wireOp",EDGE,"fa991f73-764b-433c-8341-ae9763ec17567.MirrorCS"),sQuery(id+"F0.wireOp",EDGE,"fa991f73-764b-433c-8341-ae9763ec17568.MirrorCS"),sQuery(id+"F0.wireOp",EDGE,"fa991f73-764b-433c-8341-ae9763ec17569.MirrorCS"),sQuery(id+"F0.wireOp",EDGE,"fa991f73-764b-433c-8341-ae9763ec175610.MirrorCS"),sQuery(id+"F0.wireOp",EDGE,"fa991f73-764b-433c-8341-ae9763ec175611.MirrorCS"),sQuery(id+"F0.wireOp",EDGE,"fa991f73-764b-433c-8341-ae9763ec175612.MirrorCS"),sQuery(id+"F0.wireOp",EDGE,"fa991f73-764b-433c-8341-ae9763ec175613.MirrorCS"),sQuery(id+"F0.wireOp",EDGE,"fa991f73-764b-433c-8341-ae9763ec175614.MirrorCS"),sQuery(id+"F0.wireOp",EDGE,"fa991f73-764b-433c-8341-ae9763ec175615.MirrorCS"),sQuery(id+"F0.wireOp",EDGE,"fa991f73-764b-433c-8341-ae9763ec175616.MirrorCS"),sQuery(id+"F0.wireOp",EDGE,"fa991f73-764b-433c-8341-ae9763ec175617.MirrorCS"),sQuery(id+"F0.wireOp",EDGE,"fa991f73-764b-433c-8341-ae9763ec175618.MirrorCS"),sQuery(id+"F0.wireOp",EDGE,"fa991f73-764b-433c-8341-ae9763ec175619.MirrorCS"),sQuery(id+"F0.wireOp",EDGE,"fa991f73-764b-433c-8341-ae9763ec175620.MirrorCS"),sQuery(id+"F0.wireOp",EDGE,"fa991f73-764b-433c-8341-ae9763ec175621.MirrorCS"),sQuery(id+"F0.wireOp",EDGE,"fa991f73-764b-433c-8341-ae9763ec175622.MirrorCS"),sQuery(id+"F0.wireOp",EDGE,"fa991f73-764b-433c-8341-ae9763ec175623.MirrorCS"),sQuery(id+"F0.wireOp",EDGE,"fa991f73-764b-433c-8341-ae9763ec175624.MirrorCS"),sQuery(id+"F0.wireOp",EDGE,"fa991f73-764b-433c-8341-ae9763ec175625.MirrorCS"),sQuery(id+"F0.wireOp",EDGE,"fa991f73-764b-433c-8341-ae9763ec175626.MirrorCS"),sQuery(id+"F0.wireOp",EDGE,"fa991f73-764b-433c-8341-ae9763ec175627.MirrorCS"),sQuery(id+"F0.wireOp",EDGE,"fa991f73-764b-433c-8341-ae9763ec175628.MirrorCS"),sQuery(id+"F0.wireOp",EDGE,"fa991f73-764b-433c-8341-ae9763ec175630.MirrorCS"),sQuery(id+"F0.wireOp",EDGE,"fa991f73-764b-433c-8341-ae9763ec175631.MirrorCS"),sQuery(id+"F0.wireOp",EDGE,"fa991f73-764b-433c-8341-ae9763ec175632.MirrorCS"),sQuery(id+"F0.wireOp",EDGE,"fa991f73-764b-433c-8341-ae9763ec175634.MirrorCS"),sQuery(id+"F0.wireOp",EDGE,"fa991f73-764b-433c-8341-ae9763ec175635.MirrorCS"),sQuery(id+"F0.wireOp",EDGE,"fa991f73-764b-433c-8341-ae9763ec175636.MirrorCS"),sQuery(id+"F0.wireOp",EDGE,"fa991f73-764b-433c-8341-ae9763ec175637.MirrorCS"),sQuery(id+"F0.wireOp",EDGE,"fa991f73-764b-433c-8341-ae9763ec175638.MirrorCS"),sQuery(id+"F0.wireOp",EDGE,"fa991f73-764b-433c-8341-ae9763ec175639.MirrorCS"),sQuery(id+"F0.wireOp",EDGE,"fa991f73-764b-433c-8341-ae9763ec175643.MirrorCS"),sQuery(id+"F0.wireOp",EDGE,"fa991f73-764b-433c-8341-ae9763ec175644.MirrorCS"),sQuery(id+"F0.wireOp",EDGE,"fa991f73-764b-433c-8341-ae9763ec175645.MirrorCS"),sQuery(id+"F0.wireOp",EDGE,"fa991f73-764b-433c-8341-ae9763ec175646.MirrorCS"),sQuery(id+"F0.wireOp",EDGE,"fa991f73-764b-433c-8341-ae9763ec175647.MirrorCS"),sQuery(id+"F0.wireOp",EDGE,"fa991f73-764b-433c-8341-ae9763ec175648.MirrorCS"),sQuery(id+"F0.wireOp",EDGE,"fa991f73-764b-433c-8341-ae9763ec175649.MirrorCS"),sQuery(id+"F0.wireOp",EDGE,"fa991f73-764b-433c-8341-ae9763ec175650.MirrorCS"),sQuery(id+"F0.wireOp",EDGE,"fa991f73-764b-433c-8341-ae9763ec175651.MirrorCS"),sQuery(id+"F0.wireOp",EDGE,"fa991f73-764b-433c-8341-ae9763ec175652.MirrorCS"),sQuery(id+"F0.wireOp",EDGE,"fa991f73-764b-433c-8341-ae9763ec175653.MirrorCS"),sQuery(id+"F0.wireOp",EDGE,"fa991f73-764b-433c-8341-ae9763ec175654.MirrorCS"),sQuery(id+"F0.wireOp",EDGE,"fa991f73-764b-433c-8341-ae9763ec175655.MirrorCS"),sQuery(id+"F0.wireOp",EDGE,"fa991f73-764b-433c-8341-ae9763ec175656.MirrorCS"),sQuery(id+"F0.wireOp",EDGE,"fa991f73-764b-433c-8341-ae9763ec175657.MirrorCS"),sQuery(id+"F0.wireOp",EDGE,"fa991f73-764b-433c-8341-ae9763ec175658.MirrorCS"),sQuery(id+"F0.wireOp",EDGE,"fa991f73-764b-433c-8341-ae9763ec175659.MirrorCS"),sQuery(id+"F0.wireOp",EDGE,"fa991f73-764b-433c-8341-ae9763ec175660.MirrorCS"),sQuery(id+"F0.wireOp",EDGE,"fa991f73-764b-433c-8341-ae9763ec175661.MirrorCS"),sQuery(id+"F0.wireOp",EDGE,"fa991f73-764b-433c-8341-ae9763ec175662.MirrorCS"),sQuery(id+"F0.wireOp",EDGE,"fa991f73-764b-433c-8341-ae9763ec175663.MirrorCS"),sQuery(id+"F0.wireOp",EDGE,"fa991f73-764b-433c-8341-ae9763ec175664.MirrorCS"),sQuery(id+"F0.wireOp",EDGE,"fa991f73-764b-433c-8341-ae9763ec175665.MirrorCS"),sQuery(id+"F0.wireOp",EDGE,"fa991f73-764b-433c-8341-ae9763ec175666.MirrorCS"),sQuery(id+"F0.wireOp",EDGE,"fa991f73-764b-433c-8341-ae9763ec175667.MirrorCS"),sQuery(id+"F0.wireOp",EDGE,"fa991f73-764b-433c-8341-ae9763ec175668.MirrorCS"),sQuery(id+"F0.wireOp",EDGE,"fa991f73-764b-433c-8341-ae9763ec175669.MirrorCS"),sQuery(id+"F0.wireOp",EDGE,"fa991f73-764b-433c-8341-ae9763ec175670.MirrorCS"),sQuery(id+"F0.wireOp",EDGE,"fa991f73-764b-433c-8341-ae9763ec175671.MirrorCS"),sQuery(id+"F0.wireOp",EDGE,"fa991f73-764b-433c-8341-ae9763ec175672.MirrorCS"),sQuery(id+"F0.wireOp",EDGE,"fa991f73-764b-433c-8341-ae9763ec175673.MirrorCS"),sQuery(id+"F0.wireOp",EDGE,"fa991f73-764b-433c-8341-ae9763ec175674.MirrorCS"),sQuery(id+"F0.wireOp",EDGE,"fa991f73-764b-433c-8341-ae9763ec175675.MirrorCS"),sQuery(id+"F0.wireOp",EDGE,"fa991f73-764b-433c-8341-ae9763ec175676.MirrorCS"),sQuery(id+"F0.wireOp",EDGE,"fa991f73-764b-433c-8341-ae9763ec175677.MirrorCS"),sQuery(id+"F0.wireOp",EDGE,"fa991f73-764b-433c-8341-ae9763ec175679.MirrorCS"),sQuery(id+"F0.wireOp",EDGE,"fa991f73-764b-433c-8341-ae9763ec175680.MirrorCS"),sQuery(id+"F0.wireOp",EDGE,"fa991f73-764b-433c-8341-ae9763ec175681.MirrorCS"),sQuery(id+"F0.wireOp",EDGE,"fa991f73-764b-433c-8341-ae9763ec175682.MirrorCS"),sQuery(id+"F0.wireOp",EDGE,"fa991f73-764b-433c-8341-ae9763ec175683.MirrorCS"),sQuery(id+"F0.wireOp",EDGE,"fa991f73-764b-433c-8341-ae9763ec175684.MirrorCS"),sQuery(id+"F0.wireOp",EDGE,"fa991f73-764b-433c-8341-ae9763ec175685.MirrorCS"),sQuery(id+"F0.wireOp",EDGE,"fa991f73-764b-433c-8341-ae9763ec175686.MirrorCS"),sQuery(id+"F0.wireOp",EDGE,"fa991f73-764b-433c-8341-ae9763ec175687.MirrorCS"),sQuery(id+"F0.wireOp",EDGE,"fa991f73-764b-433c-8341-ae9763ec175688.MirrorCS"),sQuery(id+"F0.wireOp",EDGE,"fa991f73-764b-433c-8341-ae9763ec175689.MirrorCS"),sQuery(id+"F0.wireOp",EDGE,"fa991f73-764b-433c-8341-ae9763ec175690.MirrorCS"),sQuery(id+"F0.wireOp",EDGE,"fa991f73-764b-433c-8341-ae9763ec175691.MirrorCS"),sQuery(id+"F0.wireOp",EDGE,"fa991f73-764b-433c-8341-ae9763ec175692.MirrorCS"),sQuery(id+"F0.wireOp",EDGE,"fa991f73-764b-433c-8341-ae9763ec175693.MirrorCS"),sQuery(id+"F0.wireOp",EDGE,"fa991f73-764b-433c-8341-ae9763ec175694.MirrorCS"),sQuery(id+"F0.wireOp",EDGE,"fa991f73-764b-433c-8341-ae9763ec175695.MirrorCS"),sQuery(id+"F0.wireOp",EDGE,"fa991f73-764b-433c-8341-ae9763ec175696.MirrorCS"),sQuery(id+"F0.wireOp",EDGE,"fa991f73-764b-433c-8341-ae9763ec175697.MirrorCS"),sQuery(id+"F0.wireOp",EDGE,"fa991f73-764b-433c-8341-ae9763ec175698.MirrorCS"),sQuery(id+"F0.wireOp",EDGE,"fa991f73-764b-433c-8341-ae9763ec175699.MirrorCS"),sQuery(id+"F0.wireOp",EDGE,"fa991f73-764b-433c-8341-ae9763ec1756100.MirrorCS"),sQuery(id+"F0.wireOp",EDGE,"fa991f73-764b-433c-8341-ae9763ec1756101.MirrorCS"),sQuery(id+"F0.wireOp",EDGE,"fa991f73-764b-433c-8341-ae9763ec1756102.MirrorCS"),sQuery(id+"F0.wireOp",EDGE,"fa991f73-764b-433c-8341-ae9763ec1756103.MirrorCS"),sQuery(id+"F0.wireOp",EDGE,"fa991f73-764b-433c-8341-ae9763ec1756104.MirrorCS"),sQuery(id+"F0.wireOp",EDGE,"fa991f73-764b-433c-8341-ae9763ec1756105.MirrorCS"),sQuery(id+"F0.wireOp",EDGE,"fa991f73-764b-433c-8341-ae9763ec1756106.MirrorCS"),sQuery(id+"F0.wireOp",EDGE,"fa991f73-764b-433c-8341-ae9763ec1756107.MirrorCS"),sQuery(id+"F0.wireOp",EDGE,"fa991f73-764b-433c-8341-ae9763ec1756108.MirrorCS"),sQuery(id+"F0.wireOp",EDGE,"fa991f73-764b-433c-8341-ae9763ec1756109.MirrorCS"),sQuery(id+"F0.wireOp",EDGE,"fa991f73-764b-433c-8341-ae9763ec1756110.MirrorCS"),sQuery(id+"F0.wireOp",EDGE,"fa991f73-764b-433c-8341-ae9763ec1756111.MirrorCS"),sQuery(id+"F0.wireOp",EDGE,"fa991f73-764b-433c-8341-ae9763ec1756112.MirrorCS"),sQuery(id+"F0.wireOp",EDGE,"fa991f73-764b-433c-8341-ae9763ec1756113.MirrorCS"),sQuery(id+"F0.wireOp",EDGE,"fa991f73-764b-433c-8341-ae9763ec1756114.MirrorCS"),sQuery(id+"F0.wireOp",EDGE,"fa991f73-764b-433c-8341-ae9763ec1756116.MirrorCS"),sQuery(id+"F0.wireOp",EDGE,"fa991f73-764b-433c-8341-ae9763ec1756117.MirrorCS"),sQuery(id+"F0.wireOp",EDGE,"fa991f73-764b-433c-8341-ae9763ec1756118.MirrorCS"),sQuery(id+"F0.wireOp",EDGE,"fa991f73-764b-433c-8341-ae9763ec1756119.MirrorCS"),sQuery(id+"F0.wireOp",EDGE,"fa991f73-764b-433c-8341-ae9763ec1756120.MirrorCS"),sQuery(id+"F0.wireOp",EDGE,"fa991f73-764b-433c-8341-ae9763ec1756121.MirrorCS"),sQuery(id+"F0.wireOp",EDGE,"fa991f73-764b-433c-8341-ae9763ec1756122.MirrorCS"),sQuery(id+"F0.wireOp",EDGE,"fa991f73-764b-433c-8341-ae9763ec1756123.MirrorCS"),sQuery(id+"F0.wireOp",EDGE,"fa991f73-764b-433c-8341-ae9763ec1756124.MirrorCS"),sQuery(id+"F0.wireOp",EDGE,"fa991f73-764b-433c-8341-ae9763ec1756125.MirrorCS"),sQuery(id+"F0.wireOp",EDGE,"fa991f73-764b-433c-8341-ae9763ec1756127.MirrorCS"),sQuery(id+"F0.wireOp",EDGE,"fa991f73-764b-433c-8341-ae9763ec1756128.MirrorCS"),sQuery(id+"F0.wireOp",EDGE,"fa991f73-764b-433c-8341-ae9763ec1756129.MirrorCS"),sQuery(id+"F0.wireOp",EDGE,"fa991f73-764b-433c-8341-ae9763ec1756130.MirrorCS"),sQuery(id+"F0.wireOp",EDGE,"fa991f73-764b-433c-8341-ae9763ec1756131.MirrorCS"),sQuery(id+"F0.wireOp",EDGE,"fa991f73-764b-433c-8341-ae9763ec1756132.MirrorCS"),sQuery(id+"F0.wireOp",EDGE,"fa991f73-764b-433c-8341-ae9763ec1756133.MirrorCS"),sQuery(id+"F0.wireOp",EDGE,"fa991f73-764b-433c-8341-ae9763ec1756134.MirrorCS"),sQuery(id+"F0.wireOp",EDGE,"fa991f73-764b-433c-8341-ae9763ec1756135.MirrorCS"),sQuery(id+"F0.wireOp",EDGE,"fa991f73-764b-433c-8341-ae9763ec1756137.MirrorCS"),sQuery(id+"F0.wireOp",EDGE,"fa991f73-764b-433c-8341-ae9763ec1756138.MirrorCS"),sQuery(id+"F0.wireOp",EDGE,"fa991f73-764b-433c-8341-ae9763ec1756139.MirrorCS"),sQuery(id+"F0.wireOp",EDGE,"fa991f73-764b-433c-8341-ae9763ec1756140.MirrorCS"),sQuery(id+"F0.wireOp",EDGE,"fa991f73-764b-433c-8341-ae9763ec1756141.MirrorCS"),sQuery(id+"F0.wireOp",EDGE,"fa991f73-764b-433c-8341-ae9763ec1756142.MirrorCS"),sQuery(id+"F0.wireOp",EDGE,"fa991f73-764b-433c-8341-ae9763ec1756143.MirrorCS"),sQuery(id+"F0.wireOp",EDGE,"fa991f73-764b-433c-8341-ae9763ec1756144.MirrorCS"),sQuery(id+"F0.wireOp",EDGE,"fa991f73-764b-433c-8341-ae9763ec1756145.MirrorCS"),sQuery(id+"F0.wireOp",EDGE,"fa991f73-764b-433c-8341-ae9763ec1756146.MirrorCS"),sQuery(id+"F0.wireOp",EDGE,"fa991f73-764b-433c-8341-ae9763ec1756147.MirrorCS"),sQuery(id+"F0.wireOp",EDGE,"fa991f73-764b-433c-8341-ae9763ec1756148.MirrorCS"),sQuery(id+"F0.wireOp",EDGE,"fa991f73-764b-433c-8341-ae9763ec1756149.MirrorCS"),sQuery(id+"F0.wireOp",EDGE,"fa991f73-764b-433c-8341-ae9763ec1756150.MirrorCS"),sQuery(id+"F0.wireOp",EDGE,"fa991f73-764b-433c-8341-ae9763ec1756151.MirrorCS"),sQuery(id+"F0.wireOp",EDGE,"fa991f73-764b-433c-8341-ae9763ec1756152.MirrorCS"),sQuery(id+"F0.wireOp",EDGE,"fa991f73-764b-433c-8341-ae9763ec1756153.MirrorCS"),sQuery(id+"F0.wireOp",EDGE,"fa991f73-764b-433c-8341-ae9763ec1756154.MirrorCS"),sQuery(id+"F0.wireOp",EDGE,"fa991f73-764b-433c-8341-ae9763ec1756155.MirrorCS"),sQuery(id+"F0.wireOp",EDGE,"fa991f73-764b-433c-8341-ae9763ec1756157.MirrorCS"),sQuery(id+"F0.wireOp",EDGE,"fa991f73-764b-433c-8341-ae9763ec1756158.MirrorCS"),sQuery(id+"F0.wireOp",EDGE,"fa991f73-764b-433c-8341-ae9763ec1756159.MirrorCS"),sQuery(id+"F0.wireOp",EDGE,"fa991f73-764b-433c-8341-ae9763ec1756160.MirrorCS"),sQuery(id+"F0.wireOp",EDGE,"fa991f73-764b-433c-8341-ae9763ec1756161.MirrorCS"),sQuery(id+"F0.wireOp",EDGE,"fa991f73-764b-433c-8341-ae9763ec1756162.MirrorCS"),sQuery(id+"F0.wireOp",EDGE,"fa991f73-764b-433c-8341-ae9763ec1756163.MirrorCS")])],"isStart":false});
            var sketch = newSketch(context, id + "F3", { "sketchPlane" : qUnion([Q0])});
            skCircle(sketch, "E427", {"center": v(24.5, 24.45) * mm, "radius": 1.25 * mm});
            skCircle(sketch, "E428", {"center": v(-24.5, 24.45) * mm, "radius": 1.25 * mm});
            skCircle(sketch, "E429", {"center": v(-24.5, -33.55) * mm, "radius": 1.25 * mm});
            skCircle(sketch, "E430", {"center": v(24.5, -33.55) * mm, "radius": 1.25 * mm});
            skSolve(sketch);
        }
        {
            var Q0;
            Q0=makeQuery(id+"F3.imprint","IMPRINT",FACE,{"disambiguationData":[TD([[makeQuery(id+"F3.imprint","IMPRINT",EDGE,{"derivedFrom":sQuery(id+"F3.wireOp",EDGE,"E427")}),-1.0]])]});
            var sketch = newSketch(context, id + "F4", { "sketchPlane" : qUnion([Q0])});
            skPoint(sketch, "E431", {"position": v(-20.32, 56.35) * mm});
            skPoint(sketch, "E432", {"position": v(-20.32, 68.3) * mm});
            skPoint(sketch, "E433", {"position": v(20.32, 56.36) * mm});
            skPoint(sketch, "E434", {"position": v(20.32, 68.32) * mm});
            skLineSegment(sketch, "E435", {"start": v(21.77, 55.1) * mm, "end": v(-21.41, 55.08) * mm});
            skLineSegment(sketch, "E436", {"start": v(-21.41, 55.08) * mm, "end": v(-21.41, 69.58) * mm});
            skLineSegment(sketch, "E437", {"start": v(-21.41, 69.58) * mm, "end": v(21.77, 69.59) * mm});
            skLineSegment(sketch, "E438", {"start": v(21.77, 69.59) * mm, "end": v(21.77, 55.1) * mm});
            skCircle(sketch, "E439", {"center": v(-20.32, 56.35) * mm, "radius": 0.6 * mm});
            skCircle(sketch, "E440", {"center": v(-20.32, 68.3) * mm, "radius": 0.6 * mm});
            skCircle(sketch, "E441", {"center": v(20.32, 68.32) * mm, "radius": 0.6 * mm});
            skCircle(sketch, "E442", {"center": v(20.32, 56.36) * mm, "radius": 0.6 * mm});
            skLineSegment(sketch, "E443", {"start": v(-20.32, 68.3) * mm, "end": v(20.32, 56.36) * mm, "construction": true});
            skLineSegment(sketch, "E444", {"start": v(20.32, 68.32) * mm, "end": v(-20.32, 56.35) * mm, "construction": true});
            skPoint(sketch, "E445", {"position": v(0, 62.33) * mm});
            skSolve(sketch);
        }
        {
            var Q0;
            Q0 = qSketchRegion(id + "F3", true);
            extrude(context, id + "F5", {"entities" : qUnion([Q0]), "operationType" : NewBodyOperationType.REMOVE, "oppositeDirection" : true, "depth" : 5 * mm, "offsetDistance" : 25 * mm});
        }
        {
            var Q0;
            Q0=makeQuery(id+"F4.imprint","IMPRINT",FACE,{"disambiguationData":[TD([[makeQuery(id+"F4.imprint","IMPRINT",EDGE,{"derivedFrom":sQuery(id+"F4.wireOp",EDGE,"E439")}),1.0]])]});
            var Q1;
            Q1=makeQuery(id+"F4.imprint","IMPRINT",FACE,{"disambiguationData":[TD([[makeQuery(id+"F4.imprint","IMPRINT",EDGE,{"derivedFrom":sQuery(id+"F4.wireOp",EDGE,"E440")}),1.0]])]});
            var Q2;
            Q2=makeQuery(id+"F4.imprint","IMPRINT",FACE,{"disambiguationData":[TD([[makeQuery(id+"F4.imprint","IMPRINT",EDGE,{"derivedFrom":sQuery(id+"F4.wireOp",EDGE,"E441")}),1.0]])]});
            var Q3;
            Q3=makeQuery(id+"F4.imprint","IMPRINT",FACE,{"disambiguationData":[TD([[makeQuery(id+"F4.imprint","IMPRINT",EDGE,{"derivedFrom":sQuery(id+"F4.wireOp",EDGE,"E442")}),1.0]])]});
            var Q4;
            Q4=sQuery(id+"F4.wireOp",EDGE,"E439");
            extrude(context, id + "F6", {"entities" : qUnion([Q0, Q1, Q2, Q3]), "operationType" : NewBodyOperationType.REMOVE, "surfaceEntities" : qUnion([Q4]), "oppositeDirection" : true, "depth" : 5 * mm, "offsetDistance" : 25 * mm});
        }
        {
            var Q0;
            Q0=makeQuery(id+"F1.opExtrude","CAP_FACE",FACE,{"disambiguationData":[OSD([sQuery(id+"F0.wireOp",EDGE,"E2"),sQuery(id+"F0.wireOp",EDGE,"E3"),sQuery(id+"F0.wireOp",EDGE,"E4"),sQuery(id+"F0.wireOp",EDGE,"E5"),sQuery(id+"F0.wireOp",EDGE,"E6.MirrorCS"),sQuery(id+"F0.wireOp",EDGE,"E7.MirrorCS"),sQuery(id+"F0.wireOp",EDGE,"E8.MirrorCS"),sQuery(id+"F0.wireOp",EDGE,"E9.MirrorCS"),sQuery(id+"F0.wireOp",EDGE,"E10.MirrorCS"),sQuery(id+"F0.wireOp",EDGE,"E11"),sQuery(id+"F0.wireOp",EDGE,"E12"),sQuery(id+"F0.wireOp",EDGE,"E14.MirrorC"),sQuery(id+"F0.wireOp",EDGE,"E15.MirrorC"),sQuery(id+"F0.wireOp",EDGE,"E16"),sQuery(id+"F0.wireOp",EDGE,"E17"),sQuery(id+"F0.wireOp",EDGE,"E18.MirrorCS"),sQuery(id+"F0.wireOp",EDGE,"E19.MirrorCS"),sQuery(id+"F0.wireOp",EDGE,"E20.MirrorCS"),sQuery(id+"F0.wireOp",EDGE,"E21.MirrorCS"),sQuery(id+"F0.wireOp",EDGE,"E22.MirrorCS"),sQuery(id+"F0.wireOp",EDGE,"E23.MirrorCS"),sQuery(id+"F0.wireOp",EDGE,"E24.MirrorCS"),sQuery(id+"F0.wireOp",EDGE,"E25.MirrorCS"),sQuery(id+"F0.wireOp",EDGE,"E26.MirrorCS"),sQuery(id+"F0.wireOp",EDGE,"E27.MirrorCS"),sQuery(id+"F0.wireOp",EDGE,"E28.MirrorCS"),sQuery(id+"F0.wireOp",EDGE,"E29.MirrorCS"),sQuery(id+"F0.wireOp",EDGE,"E30.MirrorCS"),sQuery(id+"F0.wireOp",EDGE,"E31.MirrorC"),sQuery(id+"F0.wireOp",EDGE,"E32.MirrorC"),sQuery(id+"F0.wireOp",EDGE,"E33.MirrorC"),sQuery(id+"F0.wireOp",EDGE,"E34.MirrorC"),sQuery(id+"F0.wireOp",EDGE,"68b7a1c4-8bc2-4b87-af8e-2383ff06fe301.MirrorCS"),sQuery(id+"F0.wireOp",EDGE,"68b7a1c4-8bc2-4b87-af8e-2383ff06fe302.MirrorCS"),sQuery(id+"F0.wireOp",EDGE,"68b7a1c4-8bc2-4b87-af8e-2383ff06fe303.MirrorCS"),sQuery(id+"F0.wireOp",EDGE,"68b7a1c4-8bc2-4b87-af8e-2383ff06fe304.MirrorCS"),sQuery(id+"F0.wireOp",EDGE,"68b7a1c4-8bc2-4b87-af8e-2383ff06fe305.MirrorCS"),sQuery(id+"F0.wireOp",EDGE,"68b7a1c4-8bc2-4b87-af8e-2383ff06fe306.MirrorCS"),sQuery(id+"F0.wireOp",EDGE,"68b7a1c4-8bc2-4b87-af8e-2383ff06fe307.MirrorCS"),sQuery(id+"F0.wireOp",EDGE,"68b7a1c4-8bc2-4b87-af8e-2383ff06fe308.MirrorCS"),sQuery(id+"F0.wireOp",EDGE,"68b7a1c4-8bc2-4b87-af8e-2383ff06fe309.MirrorCS"),sQuery(id+"F0.wireOp",EDGE,"68b7a1c4-8bc2-4b87-af8e-2383ff06fe3010.MirrorCS"),sQuery(id+"F0.wireOp",EDGE,"68b7a1c4-8bc2-4b87-af8e-2383ff06fe3011.MirrorCS"),sQuery(id+"F0.wireOp",EDGE,"68b7a1c4-8bc2-4b87-af8e-2383ff06fe3012.MirrorCS"),sQuery(id+"F0.wireOp",EDGE,"68b7a1c4-8bc2-4b87-af8e-2383ff06fe3013.MirrorCS"),sQuery(id+"F0.wireOp",EDGE,"68b7a1c4-8bc2-4b87-af8e-2383ff06fe3014.MirrorCS"),sQuery(id+"F0.wireOp",EDGE,"68b7a1c4-8bc2-4b87-af8e-2383ff06fe3015.MirrorCS"),sQuery(id+"F0.wireOp",EDGE,"68b7a1c4-8bc2-4b87-af8e-2383ff06fe3016.MirrorCS"),sQuery(id+"F0.wireOp",EDGE,"68b7a1c4-8bc2-4b87-af8e-2383ff06fe3017.MirrorCS"),sQuery(id+"F0.wireOp",EDGE,"68b7a1c4-8bc2-4b87-af8e-2383ff06fe3018.MirrorCS"),sQuery(id+"F0.wireOp",EDGE,"68b7a1c4-8bc2-4b87-af8e-2383ff06fe3019.MirrorCS"),sQuery(id+"F0.wireOp",EDGE,"68b7a1c4-8bc2-4b87-af8e-2383ff06fe3020.MirrorCS"),sQuery(id+"F0.wireOp",EDGE,"68b7a1c4-8bc2-4b87-af8e-2383ff06fe3021.MirrorCS"),sQuery(id+"F0.wireOp",EDGE,"68b7a1c4-8bc2-4b87-af8e-2383ff06fe3022.MirrorCS"),sQuery(id+"F0.wireOp",EDGE,"68b7a1c4-8bc2-4b87-af8e-2383ff06fe3023.MirrorCS"),sQuery(id+"F0.wireOp",EDGE,"68b7a1c4-8bc2-4b87-af8e-2383ff06fe3024.MirrorCS"),sQuery(id+"F0.wireOp",EDGE,"68b7a1c4-8bc2-4b87-af8e-2383ff06fe3025.MirrorCS"),sQuery(id+"F0.wireOp",EDGE,"68b7a1c4-8bc2-4b87-af8e-2383ff06fe3026.MirrorCS"),sQuery(id+"F0.wireOp",EDGE,"68b7a1c4-8bc2-4b87-af8e-2383ff06fe3027.MirrorCS"),sQuery(id+"F0.wireOp",EDGE,"68b7a1c4-8bc2-4b87-af8e-2383ff06fe3028.MirrorCS"),sQuery(id+"F0.wireOp",EDGE,"68b7a1c4-8bc2-4b87-af8e-2383ff06fe3029.MirrorCS"),sQuery(id+"F0.wireOp",EDGE,"68b7a1c4-8bc2-4b87-af8e-2383ff06fe3030.MirrorCS"),sQuery(id+"F0.wireOp",EDGE,"68b7a1c4-8bc2-4b87-af8e-2383ff06fe3031.MirrorCS"),sQuery(id+"F0.wireOp",EDGE,"68b7a1c4-8bc2-4b87-af8e-2383ff06fe3032.MirrorCS"),sQuery(id+"F0.wireOp",EDGE,"68b7a1c4-8bc2-4b87-af8e-2383ff06fe3033.MirrorCS"),sQuery(id+"F0.wireOp",EDGE,"68b7a1c4-8bc2-4b87-af8e-2383ff06fe3034.MirrorCS"),sQuery(id+"F0.wireOp",EDGE,"68b7a1c4-8bc2-4b87-af8e-2383ff06fe3035.MirrorCS"),sQuery(id+"F0.wireOp",EDGE,"68b7a1c4-8bc2-4b87-af8e-2383ff06fe3036.MirrorCS"),sQuery(id+"F0.wireOp",EDGE,"68b7a1c4-8bc2-4b87-af8e-2383ff06fe3037.MirrorCS"),sQuery(id+"F0.wireOp",EDGE,"68b7a1c4-8bc2-4b87-af8e-2383ff06fe3038.MirrorCS"),sQuery(id+"F0.wireOp",EDGE,"68b7a1c4-8bc2-4b87-af8e-2383ff06fe3039.MirrorCS"),sQuery(id+"F0.wireOp",EDGE,"68b7a1c4-8bc2-4b87-af8e-2383ff06fe3040.MirrorCS"),sQuery(id+"F0.wireOp",EDGE,"68b7a1c4-8bc2-4b87-af8e-2383ff06fe3041.MirrorCS"),sQuery(id+"F0.wireOp",EDGE,"68b7a1c4-8bc2-4b87-af8e-2383ff06fe3042.MirrorCS"),sQuery(id+"F0.wireOp",EDGE,"68b7a1c4-8bc2-4b87-af8e-2383ff06fe3043.MirrorCS"),sQuery(id+"F0.wireOp",EDGE,"68b7a1c4-8bc2-4b87-af8e-2383ff06fe3044.MirrorCS"),sQuery(id+"F0.wireOp",EDGE,"68b7a1c4-8bc2-4b87-af8e-2383ff06fe3045.MirrorCS"),sQuery(id+"F0.wireOp",EDGE,"68b7a1c4-8bc2-4b87-af8e-2383ff06fe3046.MirrorCS"),sQuery(id+"F0.wireOp",EDGE,"68b7a1c4-8bc2-4b87-af8e-2383ff06fe3048.MirrorCS"),sQuery(id+"F0.wireOp",EDGE,"68b7a1c4-8bc2-4b87-af8e-2383ff06fe3049.MirrorCS"),sQuery(id+"F0.wireOp",EDGE,"68b7a1c4-8bc2-4b87-af8e-2383ff06fe3050.MirrorCS"),sQuery(id+"F0.wireOp",EDGE,"68b7a1c4-8bc2-4b87-af8e-2383ff06fe3051.MirrorCS"),sQuery(id+"F0.wireOp",EDGE,"68b7a1c4-8bc2-4b87-af8e-2383ff06fe3052.MirrorCS"),sQuery(id+"F0.wireOp",EDGE,"68b7a1c4-8bc2-4b87-af8e-2383ff06fe3053.MirrorCS"),sQuery(id+"F0.wireOp",EDGE,"68b7a1c4-8bc2-4b87-af8e-2383ff06fe3054.MirrorCS"),sQuery(id+"F0.wireOp",EDGE,"68b7a1c4-8bc2-4b87-af8e-2383ff06fe3055.MirrorCS"),sQuery(id+"F0.wireOp",EDGE,"68b7a1c4-8bc2-4b87-af8e-2383ff06fe3057.MirrorCS"),sQuery(id+"F0.wireOp",EDGE,"68b7a1c4-8bc2-4b87-af8e-2383ff06fe3058.MirrorCS"),sQuery(id+"F0.wireOp",EDGE,"68b7a1c4-8bc2-4b87-af8e-2383ff06fe3059.MirrorCS"),sQuery(id+"F0.wireOp",EDGE,"68b7a1c4-8bc2-4b87-af8e-2383ff06fe3061.MirrorCS"),sQuery(id+"F0.wireOp",EDGE,"68b7a1c4-8bc2-4b87-af8e-2383ff06fe3062.MirrorCS"),sQuery(id+"F0.wireOp",EDGE,"68b7a1c4-8bc2-4b87-af8e-2383ff06fe3063.MirrorCS"),sQuery(id+"F0.wireOp",EDGE,"68b7a1c4-8bc2-4b87-af8e-2383ff06fe3064.MirrorCS"),sQuery(id+"F0.wireOp",EDGE,"68b7a1c4-8bc2-4b87-af8e-2383ff06fe3065.MirrorCS"),sQuery(id+"F0.wireOp",EDGE,"68b7a1c4-8bc2-4b87-af8e-2383ff06fe3066.MirrorCS"),sQuery(id+"F0.wireOp",EDGE,"68b7a1c4-8bc2-4b87-af8e-2383ff06fe3067.MirrorCS"),sQuery(id+"F0.wireOp",EDGE,"68b7a1c4-8bc2-4b87-af8e-2383ff06fe3068.MirrorCS"),sQuery(id+"F0.wireOp",EDGE,"68b7a1c4-8bc2-4b87-af8e-2383ff06fe3069.MirrorCS"),sQuery(id+"F0.wireOp",EDGE,"68b7a1c4-8bc2-4b87-af8e-2383ff06fe3070.MirrorCS"),sQuery(id+"F0.wireOp",EDGE,"68b7a1c4-8bc2-4b87-af8e-2383ff06fe3071.MirrorCS"),sQuery(id+"F0.wireOp",EDGE,"68b7a1c4-8bc2-4b87-af8e-2383ff06fe3072.MirrorCS"),sQuery(id+"F0.wireOp",EDGE,"68b7a1c4-8bc2-4b87-af8e-2383ff06fe3073.MirrorCS"),sQuery(id+"F0.wireOp",EDGE,"68b7a1c4-8bc2-4b87-af8e-2383ff06fe3074.MirrorCS"),sQuery(id+"F0.wireOp",EDGE,"68b7a1c4-8bc2-4b87-af8e-2383ff06fe3075.MirrorCS"),sQuery(id+"F0.wireOp",EDGE,"68b7a1c4-8bc2-4b87-af8e-2383ff06fe3076.MirrorCS"),sQuery(id+"F0.wireOp",EDGE,"68b7a1c4-8bc2-4b87-af8e-2383ff06fe3078.MirrorCS"),sQuery(id+"F0.wireOp",EDGE,"68b7a1c4-8bc2-4b87-af8e-2383ff06fe3079.MirrorCS"),sQuery(id+"F0.wireOp",EDGE,"68b7a1c4-8bc2-4b87-af8e-2383ff06fe3080.MirrorCS"),sQuery(id+"F0.wireOp",EDGE,"68b7a1c4-8bc2-4b87-af8e-2383ff06fe3081.MirrorCS"),sQuery(id+"F0.wireOp",EDGE,"68b7a1c4-8bc2-4b87-af8e-2383ff06fe3082.MirrorCS"),sQuery(id+"F0.wireOp",EDGE,"68b7a1c4-8bc2-4b87-af8e-2383ff06fe3083.MirrorCS"),sQuery(id+"F0.wireOp",EDGE,"68b7a1c4-8bc2-4b87-af8e-2383ff06fe3085.MirrorCS"),sQuery(id+"F0.wireOp",EDGE,"68b7a1c4-8bc2-4b87-af8e-2383ff06fe3086.MirrorCS"),sQuery(id+"F0.wireOp",EDGE,"68b7a1c4-8bc2-4b87-af8e-2383ff06fe3087.MirrorCS"),sQuery(id+"F0.wireOp",EDGE,"68b7a1c4-8bc2-4b87-af8e-2383ff06fe3091.MirrorCS"),sQuery(id+"F0.wireOp",EDGE,"68b7a1c4-8bc2-4b87-af8e-2383ff06fe3092.MirrorCS"),sQuery(id+"F0.wireOp",EDGE,"68b7a1c4-8bc2-4b87-af8e-2383ff06fe3094.MirrorCS"),sQuery(id+"F0.wireOp",EDGE,"68b7a1c4-8bc2-4b87-af8e-2383ff06fe3095.MirrorCS"),sQuery(id+"F0.wireOp",EDGE,"68b7a1c4-8bc2-4b87-af8e-2383ff06fe3096.MirrorCS"),sQuery(id+"F0.wireOp",EDGE,"68b7a1c4-8bc2-4b87-af8e-2383ff06fe3097.MirrorCS"),sQuery(id+"F0.wireOp",EDGE,"68b7a1c4-8bc2-4b87-af8e-2383ff06fe3098.MirrorCS"),sQuery(id+"F0.wireOp",EDGE,"68b7a1c4-8bc2-4b87-af8e-2383ff06fe3099.MirrorCS"),sQuery(id+"F0.wireOp",EDGE,"68b7a1c4-8bc2-4b87-af8e-2383ff06fe30100.MirrorCS"),sQuery(id+"F0.wireOp",EDGE,"68b7a1c4-8bc2-4b87-af8e-2383ff06fe30101.MirrorCS"),sQuery(id+"F0.wireOp",EDGE,"68b7a1c4-8bc2-4b87-af8e-2383ff06fe30102.MirrorCS"),sQuery(id+"F0.wireOp",EDGE,"68b7a1c4-8bc2-4b87-af8e-2383ff06fe30103.MirrorCS"),sQuery(id+"F0.wireOp",EDGE,"68b7a1c4-8bc2-4b87-af8e-2383ff06fe30104.MirrorCS"),sQuery(id+"F0.wireOp",EDGE,"68b7a1c4-8bc2-4b87-af8e-2383ff06fe30105.MirrorCS"),sQuery(id+"F0.wireOp",EDGE,"68b7a1c4-8bc2-4b87-af8e-2383ff06fe30106.MirrorCS"),sQuery(id+"F0.wireOp",EDGE,"68b7a1c4-8bc2-4b87-af8e-2383ff06fe30107.MirrorCS"),sQuery(id+"F0.wireOp",EDGE,"68b7a1c4-8bc2-4b87-af8e-2383ff06fe30108.MirrorCS"),sQuery(id+"F0.wireOp",EDGE,"68b7a1c4-8bc2-4b87-af8e-2383ff06fe30109.MirrorCS"),sQuery(id+"F0.wireOp",EDGE,"68b7a1c4-8bc2-4b87-af8e-2383ff06fe30111.MirrorCS"),sQuery(id+"F0.wireOp",EDGE,"68b7a1c4-8bc2-4b87-af8e-2383ff06fe30112.MirrorCS"),sQuery(id+"F0.wireOp",EDGE,"68b7a1c4-8bc2-4b87-af8e-2383ff06fe30113.MirrorCS"),sQuery(id+"F0.wireOp",EDGE,"68b7a1c4-8bc2-4b87-af8e-2383ff06fe30114.MirrorCS"),sQuery(id+"F0.wireOp",EDGE,"68b7a1c4-8bc2-4b87-af8e-2383ff06fe30115.MirrorCS"),sQuery(id+"F0.wireOp",EDGE,"68b7a1c4-8bc2-4b87-af8e-2383ff06fe30116.MirrorCS"),sQuery(id+"F0.wireOp",EDGE,"68b7a1c4-8bc2-4b87-af8e-2383ff06fe30117.MirrorCS"),sQuery(id+"F0.wireOp",EDGE,"68b7a1c4-8bc2-4b87-af8e-2383ff06fe30118.MirrorCS"),sQuery(id+"F0.wireOp",EDGE,"68b7a1c4-8bc2-4b87-af8e-2383ff06fe30119.MirrorCS"),sQuery(id+"F0.wireOp",EDGE,"68b7a1c4-8bc2-4b87-af8e-2383ff06fe30120.MirrorCS"),sQuery(id+"F0.wireOp",EDGE,"68b7a1c4-8bc2-4b87-af8e-2383ff06fe30121.MirrorCS"),sQuery(id+"F0.wireOp",EDGE,"68b7a1c4-8bc2-4b87-af8e-2383ff06fe30122.MirrorCS"),sQuery(id+"F0.wireOp",EDGE,"68b7a1c4-8bc2-4b87-af8e-2383ff06fe30123.MirrorCS"),sQuery(id+"F0.wireOp",EDGE,"68b7a1c4-8bc2-4b87-af8e-2383ff06fe30124.MirrorCS"),sQuery(id+"F0.wireOp",EDGE,"68b7a1c4-8bc2-4b87-af8e-2383ff06fe30125.MirrorCS"),sQuery(id+"F0.wireOp",EDGE,"68b7a1c4-8bc2-4b87-af8e-2383ff06fe30126.MirrorCS"),sQuery(id+"F0.wireOp",EDGE,"68b7a1c4-8bc2-4b87-af8e-2383ff06fe30127.MirrorCS"),sQuery(id+"F0.wireOp",EDGE,"68b7a1c4-8bc2-4b87-af8e-2383ff06fe30128.MirrorCS"),sQuery(id+"F0.wireOp",EDGE,"68b7a1c4-8bc2-4b87-af8e-2383ff06fe30129.MirrorCS"),sQuery(id+"F0.wireOp",EDGE,"68b7a1c4-8bc2-4b87-af8e-2383ff06fe30130.MirrorCS"),sQuery(id+"F0.wireOp",EDGE,"68b7a1c4-8bc2-4b87-af8e-2383ff06fe30131.MirrorCS"),sQuery(id+"F0.wireOp",EDGE,"68b7a1c4-8bc2-4b87-af8e-2383ff06fe30132.MirrorCS"),sQuery(id+"F0.wireOp",EDGE,"68b7a1c4-8bc2-4b87-af8e-2383ff06fe30133.MirrorCS"),sQuery(id+"F0.wireOp",EDGE,"68b7a1c4-8bc2-4b87-af8e-2383ff06fe30134.MirrorCS"),sQuery(id+"F0.wireOp",EDGE,"68b7a1c4-8bc2-4b87-af8e-2383ff06fe30135.MirrorCS"),sQuery(id+"F0.wireOp",EDGE,"68b7a1c4-8bc2-4b87-af8e-2383ff06fe30136.MirrorCS"),sQuery(id+"F0.wireOp",EDGE,"68b7a1c4-8bc2-4b87-af8e-2383ff06fe30137.MirrorCS"),sQuery(id+"F0.wireOp",EDGE,"68b7a1c4-8bc2-4b87-af8e-2383ff06fe30138.MirrorCS"),sQuery(id+"F0.wireOp",EDGE,"68b7a1c4-8bc2-4b87-af8e-2383ff06fe30139.MirrorCS"),sQuery(id+"F0.wireOp",EDGE,"68b7a1c4-8bc2-4b87-af8e-2383ff06fe30140.MirrorCS"),sQuery(id+"F0.wireOp",EDGE,"68b7a1c4-8bc2-4b87-af8e-2383ff06fe30141.MirrorCS"),sQuery(id+"F0.wireOp",EDGE,"68b7a1c4-8bc2-4b87-af8e-2383ff06fe30142.MirrorCS"),sQuery(id+"F0.wireOp",EDGE,"68b7a1c4-8bc2-4b87-af8e-2383ff06fe30143.MirrorCS"),sQuery(id+"F0.wireOp",EDGE,"68b7a1c4-8bc2-4b87-af8e-2383ff06fe30145.MirrorCS"),sQuery(id+"F0.wireOp",EDGE,"68b7a1c4-8bc2-4b87-af8e-2383ff06fe30146.MirrorCS"),sQuery(id+"F0.wireOp",EDGE,"68b7a1c4-8bc2-4b87-af8e-2383ff06fe30147.MirrorCS"),sQuery(id+"F0.wireOp",EDGE,"68b7a1c4-8bc2-4b87-af8e-2383ff06fe30148.MirrorCS"),sQuery(id+"F0.wireOp",EDGE,"68b7a1c4-8bc2-4b87-af8e-2383ff06fe30149.MirrorCS"),sQuery(id+"F0.wireOp",EDGE,"68b7a1c4-8bc2-4b87-af8e-2383ff06fe30150.MirrorCS"),sQuery(id+"F0.wireOp",EDGE,"68b7a1c4-8bc2-4b87-af8e-2383ff06fe30151.MirrorCS"),sQuery(id+"F0.wireOp",EDGE,"68b7a1c4-8bc2-4b87-af8e-2383ff06fe30152.MirrorCS"),sQuery(id+"F0.wireOp",EDGE,"68b7a1c4-8bc2-4b87-af8e-2383ff06fe30153.MirrorCS"),sQuery(id+"F0.wireOp",EDGE,"68b7a1c4-8bc2-4b87-af8e-2383ff06fe30154.MirrorCS"),sQuery(id+"F0.wireOp",EDGE,"68b7a1c4-8bc2-4b87-af8e-2383ff06fe30155.MirrorCS"),sQuery(id+"F0.wireOp",EDGE,"68b7a1c4-8bc2-4b87-af8e-2383ff06fe30156.MirrorCS"),sQuery(id+"F0.wireOp",EDGE,"68b7a1c4-8bc2-4b87-af8e-2383ff06fe30157.MirrorCS"),sQuery(id+"F0.wireOp",EDGE,"68b7a1c4-8bc2-4b87-af8e-2383ff06fe30158.MirrorCS"),sQuery(id+"F0.wireOp",EDGE,"68b7a1c4-8bc2-4b87-af8e-2383ff06fe30159.MirrorCS"),sQuery(id+"F0.wireOp",EDGE,"68b7a1c4-8bc2-4b87-af8e-2383ff06fe30160.MirrorCS"),sQuery(id+"F0.wireOp",EDGE,"68b7a1c4-8bc2-4b87-af8e-2383ff06fe30161.MirrorCS"),sQuery(id+"F0.wireOp",EDGE,"68b7a1c4-8bc2-4b87-af8e-2383ff06fe30162.MirrorCS"),sQuery(id+"F0.wireOp",EDGE,"68b7a1c4-8bc2-4b87-af8e-2383ff06fe30163.MirrorCS"),sQuery(id+"F0.wireOp",EDGE,"b9f1c8b0-1812-4977-8847-28bb21a96fe669.MirrorCS"),sQuery(id+"F0.wireOp",EDGE,"b9f1c8b0-1812-4977-8847-28bb21a96fe670.MirrorCS"),sQuery(id+"F0.wireOp",EDGE,"b9f1c8b0-1812-4977-8847-28bb21a96fe671.MirrorCS"),sQuery(id+"F0.wireOp",EDGE,"b9f1c8b0-1812-4977-8847-28bb21a96fe672.MirrorCS"),sQuery(id+"F0.wireOp",EDGE,"b9f1c8b0-1812-4977-8847-28bb21a96fe673.MirrorCS"),sQuery(id+"F0.wireOp",EDGE,"b9f1c8b0-1812-4977-8847-28bb21a96fe674.MirrorCS"),sQuery(id+"F0.wireOp",EDGE,"b9f1c8b0-1812-4977-8847-28bb21a96fe675.MirrorCS"),sQuery(id+"F0.wireOp",EDGE,"b9f1c8b0-1812-4977-8847-28bb21a96fe676.MirrorCS"),sQuery(id+"F0.wireOp",EDGE,"b9f1c8b0-1812-4977-8847-28bb21a96fe677.MirrorCS"),sQuery(id+"F0.wireOp",EDGE,"b9f1c8b0-1812-4977-8847-28bb21a96fe678.MirrorCS"),sQuery(id+"F0.wireOp",EDGE,"b9f1c8b0-1812-4977-8847-28bb21a96fe679.MirrorCS"),sQuery(id+"F0.wireOp",EDGE,"b9f1c8b0-1812-4977-8847-28bb21a96fe681.MirrorCS"),sQuery(id+"F0.wireOp",EDGE,"b9f1c8b0-1812-4977-8847-28bb21a96fe682.MirrorCS"),sQuery(id+"F0.wireOp",EDGE,"b9f1c8b0-1812-4977-8847-28bb21a96fe683.MirrorCS"),sQuery(id+"F0.wireOp",EDGE,"b9f1c8b0-1812-4977-8847-28bb21a96fe684.MirrorCS"),sQuery(id+"F0.wireOp",EDGE,"b9f1c8b0-1812-4977-8847-28bb21a96fe685.MirrorCS"),sQuery(id+"F0.wireOp",EDGE,"b9f1c8b0-1812-4977-8847-28bb21a96fe686.MirrorCS"),sQuery(id+"F0.wireOp",EDGE,"b9f1c8b0-1812-4977-8847-28bb21a96fe688.MirrorCS"),sQuery(id+"F0.wireOp",EDGE,"b9f1c8b0-1812-4977-8847-28bb21a96fe689.MirrorCS"),sQuery(id+"F0.wireOp",EDGE,"b9f1c8b0-1812-4977-8847-28bb21a96fe690.MirrorCS"),sQuery(id+"F0.wireOp",EDGE,"b9f1c8b0-1812-4977-8847-28bb21a96fe691.MirrorCS"),sQuery(id+"F0.wireOp",EDGE,"b9f1c8b0-1812-4977-8847-28bb21a96fe692.MirrorCS"),sQuery(id+"F0.wireOp",EDGE,"b9f1c8b0-1812-4977-8847-28bb21a96fe693.MirrorCS"),sQuery(id+"F0.wireOp",EDGE,"b9f1c8b0-1812-4977-8847-28bb21a96fe694.MirrorCS"),sQuery(id+"F0.wireOp",EDGE,"b9f1c8b0-1812-4977-8847-28bb21a96fe695.MirrorCS"),sQuery(id+"F0.wireOp",EDGE,"b9f1c8b0-1812-4977-8847-28bb21a96fe696.MirrorCS"),sQuery(id+"F0.wireOp",EDGE,"b9f1c8b0-1812-4977-8847-28bb21a96fe697.MirrorCS"),sQuery(id+"F0.wireOp",EDGE,"b9f1c8b0-1812-4977-8847-28bb21a96fe698.MirrorCS"),sQuery(id+"F0.wireOp",EDGE,"b9f1c8b0-1812-4977-8847-28bb21a96fe699.MirrorCS"),sQuery(id+"F0.wireOp",EDGE,"b9f1c8b0-1812-4977-8847-28bb21a96fe6100.MirrorCS"),sQuery(id+"F0.wireOp",EDGE,"b9f1c8b0-1812-4977-8847-28bb21a96fe6101.MirrorCS"),sQuery(id+"F0.wireOp",EDGE,"b9f1c8b0-1812-4977-8847-28bb21a96fe6103.MirrorCS"),sQuery(id+"F0.wireOp",EDGE,"b9f1c8b0-1812-4977-8847-28bb21a96fe6104.MirrorCS"),sQuery(id+"F0.wireOp",EDGE,"b9f1c8b0-1812-4977-8847-28bb21a96fe6105.MirrorCS"),sQuery(id+"F0.wireOp",EDGE,"b9f1c8b0-1812-4977-8847-28bb21a96fe6106.MirrorCS"),sQuery(id+"F0.wireOp",EDGE,"b9f1c8b0-1812-4977-8847-28bb21a96fe6107.MirrorCS"),sQuery(id+"F0.wireOp",EDGE,"b9f1c8b0-1812-4977-8847-28bb21a96fe6108.MirrorCS"),sQuery(id+"F0.wireOp",EDGE,"b9f1c8b0-1812-4977-8847-28bb21a96fe6109.MirrorCS"),sQuery(id+"F0.wireOp",EDGE,"b9f1c8b0-1812-4977-8847-28bb21a96fe6111.MirrorCS"),sQuery(id+"F0.wireOp",EDGE,"b9f1c8b0-1812-4977-8847-28bb21a96fe6112.MirrorCS"),sQuery(id+"F0.wireOp",EDGE,"b9f1c8b0-1812-4977-8847-28bb21a96fe6114.MirrorCS"),sQuery(id+"F0.wireOp",EDGE,"b9f1c8b0-1812-4977-8847-28bb21a96fe6115.MirrorCS"),sQuery(id+"F0.wireOp",EDGE,"b9f1c8b0-1812-4977-8847-28bb21a96fe6116.MirrorCS"),sQuery(id+"F0.wireOp",EDGE,"b9f1c8b0-1812-4977-8847-28bb21a96fe6117.MirrorCS"),sQuery(id+"F0.wireOp",EDGE,"b9f1c8b0-1812-4977-8847-28bb21a96fe6118.MirrorCS"),sQuery(id+"F0.wireOp",EDGE,"b9f1c8b0-1812-4977-8847-28bb21a96fe6119.MirrorCS"),sQuery(id+"F0.wireOp",EDGE,"b9f1c8b0-1812-4977-8847-28bb21a96fe6120.MirrorCS"),sQuery(id+"F0.wireOp",EDGE,"b9f1c8b0-1812-4977-8847-28bb21a96fe6121.MirrorCS"),sQuery(id+"F0.wireOp",EDGE,"b9f1c8b0-1812-4977-8847-28bb21a96fe6122.MirrorCS"),sQuery(id+"F0.wireOp",EDGE,"b9f1c8b0-1812-4977-8847-28bb21a96fe6123.MirrorCS"),sQuery(id+"F0.wireOp",EDGE,"b9f1c8b0-1812-4977-8847-28bb21a96fe6124.MirrorCS"),sQuery(id+"F0.wireOp",EDGE,"b9f1c8b0-1812-4977-8847-28bb21a96fe6125.MirrorCS"),sQuery(id+"F0.wireOp",EDGE,"b9f1c8b0-1812-4977-8847-28bb21a96fe6126.MirrorCS"),sQuery(id+"F0.wireOp",EDGE,"b9f1c8b0-1812-4977-8847-28bb21a96fe6127.MirrorCS"),sQuery(id+"F0.wireOp",EDGE,"b9f1c8b0-1812-4977-8847-28bb21a96fe6128.MirrorCS"),sQuery(id+"F0.wireOp",EDGE,"b9f1c8b0-1812-4977-8847-28bb21a96fe6129.MirrorCS"),sQuery(id+"F0.wireOp",EDGE,"b9f1c8b0-1812-4977-8847-28bb21a96fe6131.MirrorCS"),sQuery(id+"F0.wireOp",EDGE,"b9f1c8b0-1812-4977-8847-28bb21a96fe6132.MirrorCS"),sQuery(id+"F0.wireOp",EDGE,"b9f1c8b0-1812-4977-8847-28bb21a96fe6133.MirrorCS"),sQuery(id+"F0.wireOp",EDGE,"b9f1c8b0-1812-4977-8847-28bb21a96fe6135.MirrorCS"),sQuery(id+"F0.wireOp",EDGE,"b9f1c8b0-1812-4977-8847-28bb21a96fe6136.MirrorCS"),sQuery(id+"F0.wireOp",EDGE,"b9f1c8b0-1812-4977-8847-28bb21a96fe6137.MirrorCS"),sQuery(id+"F0.wireOp",EDGE,"b9f1c8b0-1812-4977-8847-28bb21a96fe6138.MirrorCS"),sQuery(id+"F0.wireOp",EDGE,"b9f1c8b0-1812-4977-8847-28bb21a96fe6140.MirrorCS"),sQuery(id+"F0.wireOp",EDGE,"b9f1c8b0-1812-4977-8847-28bb21a96fe6144.MirrorCS"),sQuery(id+"F0.wireOp",EDGE,"b9f1c8b0-1812-4977-8847-28bb21a96fe6147.MirrorCS"),sQuery(id+"F0.wireOp",EDGE,"b9f1c8b0-1812-4977-8847-28bb21a96fe6179.MirrorCS"),sQuery(id+"F0.wireOp",EDGE,"b9f1c8b0-1812-4977-8847-28bb21a96fe6184.MirrorCS"),sQuery(id+"F0.wireOp",EDGE,"b9f1c8b0-1812-4977-8847-28bb21a96fe6240.MirrorCS"),sQuery(id+"F0.wireOp",EDGE,"b9f1c8b0-1812-4977-8847-28bb21a96fe6241.MirrorCS"),sQuery(id+"F0.wireOp",EDGE,"b9f1c8b0-1812-4977-8847-28bb21a96fe6242.MirrorCS"),sQuery(id+"F0.wireOp",EDGE,"b9f1c8b0-1812-4977-8847-28bb21a96fe6243.MirrorCS"),sQuery(id+"F0.wireOp",EDGE,"b9f1c8b0-1812-4977-8847-28bb21a96fe6244.MirrorCS"),sQuery(id+"F0.wireOp",EDGE,"b9f1c8b0-1812-4977-8847-28bb21a96fe6245.MirrorCS"),sQuery(id+"F0.wireOp",EDGE,"b9f1c8b0-1812-4977-8847-28bb21a96fe6246.MirrorCS"),sQuery(id+"F0.wireOp",EDGE,"b9f1c8b0-1812-4977-8847-28bb21a96fe6247.MirrorCS"),sQuery(id+"F0.wireOp",EDGE,"b9f1c8b0-1812-4977-8847-28bb21a96fe6248.MirrorCS"),sQuery(id+"F0.wireOp",EDGE,"b9f1c8b0-1812-4977-8847-28bb21a96fe6250.MirrorCS"),sQuery(id+"F0.wireOp",EDGE,"b9f1c8b0-1812-4977-8847-28bb21a96fe6251.MirrorCS"),sQuery(id+"F0.wireOp",EDGE,"b9f1c8b0-1812-4977-8847-28bb21a96fe6252.MirrorCS"),sQuery(id+"F0.wireOp",EDGE,"b9f1c8b0-1812-4977-8847-28bb21a96fe6253.MirrorCS"),sQuery(id+"F0.wireOp",EDGE,"b9f1c8b0-1812-4977-8847-28bb21a96fe6254.MirrorCS"),sQuery(id+"F0.wireOp",EDGE,"b9f1c8b0-1812-4977-8847-28bb21a96fe6255.MirrorCS"),sQuery(id+"F0.wireOp",EDGE,"b9f1c8b0-1812-4977-8847-28bb21a96fe6256.MirrorCS"),sQuery(id+"F0.wireOp",EDGE,"b9f1c8b0-1812-4977-8847-28bb21a96fe6257.MirrorCS"),sQuery(id+"F0.wireOp",EDGE,"b9f1c8b0-1812-4977-8847-28bb21a96fe6258.MirrorCS"),sQuery(id+"F0.wireOp",EDGE,"b9f1c8b0-1812-4977-8847-28bb21a96fe6259.MirrorCS"),sQuery(id+"F0.wireOp",EDGE,"b9f1c8b0-1812-4977-8847-28bb21a96fe6260.MirrorCS"),sQuery(id+"F0.wireOp",EDGE,"b9f1c8b0-1812-4977-8847-28bb21a96fe6261.MirrorCS"),sQuery(id+"F0.wireOp",EDGE,"b9f1c8b0-1812-4977-8847-28bb21a96fe6262.MirrorCS"),sQuery(id+"F0.wireOp",EDGE,"b9f1c8b0-1812-4977-8847-28bb21a96fe6263.MirrorCS"),sQuery(id+"F0.wireOp",EDGE,"b9f1c8b0-1812-4977-8847-28bb21a96fe6264.MirrorCS"),sQuery(id+"F0.wireOp",EDGE,"b9f1c8b0-1812-4977-8847-28bb21a96fe6265.MirrorCS"),sQuery(id+"F0.wireOp",EDGE,"b9f1c8b0-1812-4977-8847-28bb21a96fe6266.MirrorCS"),sQuery(id+"F0.wireOp",EDGE,"b9f1c8b0-1812-4977-8847-28bb21a96fe6267.MirrorCS"),sQuery(id+"F0.wireOp",EDGE,"b9f1c8b0-1812-4977-8847-28bb21a96fe6268.MirrorCS"),sQuery(id+"F0.wireOp",EDGE,"b9f1c8b0-1812-4977-8847-28bb21a96fe6269.MirrorCS"),sQuery(id+"F0.wireOp",EDGE,"b9f1c8b0-1812-4977-8847-28bb21a96fe6270.MirrorCS"),sQuery(id+"F0.wireOp",EDGE,"b9f1c8b0-1812-4977-8847-28bb21a96fe6271.MirrorCS"),sQuery(id+"F0.wireOp",EDGE,"b9f1c8b0-1812-4977-8847-28bb21a96fe6272.MirrorCS"),sQuery(id+"F0.wireOp",EDGE,"b9f1c8b0-1812-4977-8847-28bb21a96fe6274.MirrorCS"),sQuery(id+"F0.wireOp",EDGE,"b9f1c8b0-1812-4977-8847-28bb21a96fe6275.MirrorCS"),sQuery(id+"F0.wireOp",EDGE,"b9f1c8b0-1812-4977-8847-28bb21a96fe6276.MirrorCS"),sQuery(id+"F0.wireOp",EDGE,"b9f1c8b0-1812-4977-8847-28bb21a96fe6277.MirrorCS"),sQuery(id+"F0.wireOp",EDGE,"b9f1c8b0-1812-4977-8847-28bb21a96fe6278.MirrorCS"),sQuery(id+"F0.wireOp",EDGE,"b9f1c8b0-1812-4977-8847-28bb21a96fe6279.MirrorCS"),sQuery(id+"F0.wireOp",EDGE,"b9f1c8b0-1812-4977-8847-28bb21a96fe6280.MirrorCS"),sQuery(id+"F0.wireOp",EDGE,"b9f1c8b0-1812-4977-8847-28bb21a96fe6281.MirrorCS"),sQuery(id+"F0.wireOp",EDGE,"b9f1c8b0-1812-4977-8847-28bb21a96fe6282.MirrorCS"),sQuery(id+"F0.wireOp",EDGE,"b9f1c8b0-1812-4977-8847-28bb21a96fe6283.MirrorCS"),sQuery(id+"F0.wireOp",EDGE,"b9f1c8b0-1812-4977-8847-28bb21a96fe6284.MirrorCS"),sQuery(id+"F0.wireOp",EDGE,"b9f1c8b0-1812-4977-8847-28bb21a96fe6286.MirrorCS"),sQuery(id+"F0.wireOp",EDGE,"b9f1c8b0-1812-4977-8847-28bb21a96fe6287.MirrorCS"),sQuery(id+"F0.wireOp",EDGE,"b9f1c8b0-1812-4977-8847-28bb21a96fe6288.MirrorCS"),sQuery(id+"F0.wireOp",EDGE,"b9f1c8b0-1812-4977-8847-28bb21a96fe6289.MirrorCS"),sQuery(id+"F0.wireOp",EDGE,"b9f1c8b0-1812-4977-8847-28bb21a96fe6290.MirrorCS"),sQuery(id+"F0.wireOp",EDGE,"b9f1c8b0-1812-4977-8847-28bb21a96fe6291.MirrorCS"),sQuery(id+"F0.wireOp",EDGE,"b9f1c8b0-1812-4977-8847-28bb21a96fe6292.MirrorCS"),sQuery(id+"F0.wireOp",EDGE,"b9f1c8b0-1812-4977-8847-28bb21a96fe6293.MirrorCS"),sQuery(id+"F0.wireOp",EDGE,"b9f1c8b0-1812-4977-8847-28bb21a96fe6294.MirrorCS"),sQuery(id+"F0.wireOp",EDGE,"b9f1c8b0-1812-4977-8847-28bb21a96fe6295.MirrorCS"),sQuery(id+"F0.wireOp",EDGE,"b9f1c8b0-1812-4977-8847-28bb21a96fe6296.MirrorCS"),sQuery(id+"F0.wireOp",EDGE,"b9f1c8b0-1812-4977-8847-28bb21a96fe6298.MirrorCS"),sQuery(id+"F0.wireOp",EDGE,"b9f1c8b0-1812-4977-8847-28bb21a96fe6299.MirrorCS"),sQuery(id+"F0.wireOp",EDGE,"b9f1c8b0-1812-4977-8847-28bb21a96fe6300.MirrorCS"),sQuery(id+"F0.wireOp",EDGE,"b9f1c8b0-1812-4977-8847-28bb21a96fe6301.MirrorCS"),sQuery(id+"F0.wireOp",EDGE,"b9f1c8b0-1812-4977-8847-28bb21a96fe6302.MirrorCS"),sQuery(id+"F0.wireOp",EDGE,"b9f1c8b0-1812-4977-8847-28bb21a96fe6303.MirrorCS"),sQuery(id+"F0.wireOp",EDGE,"b9f1c8b0-1812-4977-8847-28bb21a96fe6304.MirrorCS"),sQuery(id+"F0.wireOp",EDGE,"b9f1c8b0-1812-4977-8847-28bb21a96fe6305.MirrorCS"),sQuery(id+"F0.wireOp",EDGE,"b9f1c8b0-1812-4977-8847-28bb21a96fe6306.MirrorCS"),sQuery(id+"F0.wireOp",EDGE,"b9f1c8b0-1812-4977-8847-28bb21a96fe6309.MirrorCS"),sQuery(id+"F0.wireOp",EDGE,"b9f1c8b0-1812-4977-8847-28bb21a96fe6310.MirrorCS"),sQuery(id+"F0.wireOp",EDGE,"b9f1c8b0-1812-4977-8847-28bb21a96fe6311.MirrorCS"),sQuery(id+"F0.wireOp",EDGE,"b9f1c8b0-1812-4977-8847-28bb21a96fe6312.MirrorCS"),sQuery(id+"F0.wireOp",EDGE,"b9f1c8b0-1812-4977-8847-28bb21a96fe6313.MirrorCS"),sQuery(id+"F0.wireOp",EDGE,"b9f1c8b0-1812-4977-8847-28bb21a96fe6314.MirrorCS"),sQuery(id+"F0.wireOp",EDGE,"b9f1c8b0-1812-4977-8847-28bb21a96fe6315.MirrorCS"),sQuery(id+"F0.wireOp",EDGE,"b9f1c8b0-1812-4977-8847-28bb21a96fe6316.MirrorCS"),sQuery(id+"F0.wireOp",EDGE,"b9f1c8b0-1812-4977-8847-28bb21a96fe6317.MirrorCS"),sQuery(id+"F0.wireOp",EDGE,"b9f1c8b0-1812-4977-8847-28bb21a96fe6318.MirrorCS"),sQuery(id+"F0.wireOp",EDGE,"b9f1c8b0-1812-4977-8847-28bb21a96fe6319.MirrorCS"),sQuery(id+"F0.wireOp",EDGE,"b9f1c8b0-1812-4977-8847-28bb21a96fe6320.MirrorCS"),sQuery(id+"F0.wireOp",EDGE,"b9f1c8b0-1812-4977-8847-28bb21a96fe6321.MirrorCS"),sQuery(id+"F0.wireOp",EDGE,"b9f1c8b0-1812-4977-8847-28bb21a96fe6322.MirrorCS"),sQuery(id+"F0.wireOp",EDGE,"b9f1c8b0-1812-4977-8847-28bb21a96fe6323.MirrorCS"),sQuery(id+"F0.wireOp",EDGE,"b9f1c8b0-1812-4977-8847-28bb21a96fe6324.MirrorCS"),sQuery(id+"F0.wireOp",EDGE,"b9f1c8b0-1812-4977-8847-28bb21a96fe6326.MirrorCS"),sQuery(id+"F0.wireOp",EDGE,"1b0cb521-1372-4fad-a006-b8d427d7732a4.MirrorCS"),sQuery(id+"F0.wireOp",EDGE,"1b0cb521-1372-4fad-a006-b8d427d7732a5.MirrorCS"),sQuery(id+"F0.wireOp",EDGE,"1b0cb521-1372-4fad-a006-b8d427d7732a6.MirrorCS"),sQuery(id+"F0.wireOp",EDGE,"1b0cb521-1372-4fad-a006-b8d427d7732a7.MirrorCS")])],"isStart":true});
            var sketch = newSketch(context, id + "F7", { "sketchPlane" : qUnion([Q0])});
            skCircle(sketch, "E446", {"center": v(24.5, 33.55) * mm, "radius": 3 * mm});
            skCircle(sketch, "E447", {"center": v(-24.5, 33.55) * mm, "radius": 3 * mm});
            skCircle(sketch, "E448", {"center": v(-24.5, -24.45) * mm, "radius": 3 * mm});
            skCircle(sketch, "E449", {"center": v(24.5, -24.45) * mm, "radius": 3 * mm});
            skCircle(sketch, "E450", {"center": v(20.32, -56.36) * mm, "radius": 1.5 * mm});
            skCircle(sketch, "E451", {"center": v(-20.32, -56.35) * mm, "radius": 1.5 * mm});
            skCircle(sketch, "E452", {"center": v(-20.32, -68.3) * mm, "radius": 1.5 * mm});
            skCircle(sketch, "E453", {"center": v(20.32, -68.32) * mm, "radius": 1.5 * mm});
            skCircle(sketch, "E454", {"center": v(-24.5, -24.45) * mm, "radius": 1.25 * mm});
            skCircle(sketch, "E455", {"center": v(-20.32, -56.35) * mm, "radius": 0.6 * mm});
            skPoint(sketch, "E455.first.point", {"position": v(-20.16, -55.77) * mm});
            skPoint(sketch, "E455.second.point", {"position": v(-20.29, -56.95) * mm});
            skPoint(sketch, "E455.third.point", {"position": v(-20.29, -56.95) * mm});
            skCircle(sketch, "E456", {"center": v(-20.32, -68.3) * mm, "radius": 0.6 * mm});
            skPoint(sketch, "E456.first.point", {"position": v(-20.32, -68.9) * mm});
            skPoint(sketch, "E456.second.point", {"position": v(-19.72, -68.3) * mm});
            skPoint(sketch, "E456.third.point", {"position": v(-20.32, -68.9) * mm});
            skCircle(sketch, "E457", {"center": v(20.32, -56.36) * mm, "radius": 0.6 * mm});
            skPoint(sketch, "E457.first.point", {"position": v(20.44, -56.95) * mm});
            skPoint(sketch, "E457.second.point", {"position": v(20.21, -55.77) * mm});
            skPoint(sketch, "E457.third.point", {"position": v(20.44, -56.95) * mm});
            skCircle(sketch, "E458", {"center": v(20.32, -68.32) * mm, "radius": 0.6 * mm});
            skPoint(sketch, "E458.first.point", {"position": v(20.32, -67.72) * mm});
            skPoint(sketch, "E458.second.point", {"position": v(20.32, -67.72) * mm});
            skPoint(sketch, "E458.third.point", {"position": v(20.23, -67.72) * mm});
            skCircle(sketch, "E459", {"center": v(24.6, -24.45) * mm, "radius": 1.25 * mm});
            skPoint(sketch, "E459.first.point", {"position": v(24.59, -23.2) * mm});
            skPoint(sketch, "E459.second.point", {"position": v(24.52, -25.7) * mm});
            skPoint(sketch, "E459.third.point", {"position": v(24.52, -25.7) * mm});
            skCircle(sketch, "E460", {"center": v(24.5, 33.55) * mm, "radius": 1.25 * mm});
            skPoint(sketch, "E460.first.point", {"position": v(24.53, 32.3) * mm});
            skPoint(sketch, "E460.second.point", {"position": v(24.53, 32.3) * mm});
            skPoint(sketch, "E460.third.point", {"position": v(24.41, 32.3) * mm});
            skCircle(sketch, "E461", {"center": v(-24.51, 36.04) * mm, "radius": 1.25 * mm});
            skPoint(sketch, "E461.first.point", {"position": v(-24.59, 34.8) * mm});
            skPoint(sketch, "E461.second.point", {"position": v(-24.42, 34.8) * mm});
            skPoint(sketch, "E461.third.point", {"position": v(-24.42, 34.8) * mm});
            skSolve(sketch);
        }
        {
            var Q0;
            Q0=makeQuery(id+"F7.imprint","IMPRINT",FACE,{"disambiguationData":[TD([[makeQuery(id+"F7.imprint","IMPRINT",EDGE,{"derivedFrom":sQuery(id+"F7.wireOp",EDGE,"E449")}),1.0]])]});
            var Q1;
            Q1=makeQuery(id+"F7.imprint","IMPRINT",FACE,{"disambiguationData":[TD([[makeQuery(id+"F7.imprint","IMPRINT",EDGE,{"derivedFrom":sQuery(id+"F7.wireOp",EDGE,"E448")}),1.0]])]});
            var Q2;
            Q2=makeQuery(id+"F7.imprint","IMPRINT",FACE,{"disambiguationData":[TD([[makeQuery(id+"F7.imprint","IMPRINT",EDGE,{"derivedFrom":sQuery(id+"F7.wireOp",EDGE,"E446")}),1.0]])]});
            var Q3;
            Q3=makeQuery(id+"F7.imprint","IMPRINT",FACE,{"disambiguationData":[TD([[makeQuery(id+"F7.imprint","IMPRINT",EDGE,{"derivedFrom":sQuery(id+"F7.wireOp",EDGE,"E447")}),1.0]])]});
            extrude(context, id + "F8", {"entities" : qUnion([Q0, Q1, Q2, Q3]), "operationType" : NewBodyOperationType.ADD, "depth" : 3 * mm, "offsetDistance" : 25 * mm});
        }
        {
            var Q0;
            Q0=makeQuery(id+"F7.imprint","IMPRINT",FACE,{"disambiguationData":[TD([[makeQuery(id+"F7.imprint","IMPRINT",EDGE,{"derivedFrom":sQuery(id+"F7.wireOp",EDGE,"E450")}),1.0]])]});
            var Q1;
            Q1=makeQuery(id+"F7.imprint","IMPRINT",FACE,{"disambiguationData":[TD([[makeQuery(id+"F7.imprint","IMPRINT",EDGE,{"derivedFrom":sQuery(id+"F7.wireOp",EDGE,"E453")}),1.0]])]});
            var Q2;
            Q2=makeQuery(id+"F7.imprint","IMPRINT",FACE,{"disambiguationData":[TD([[makeQuery(id+"F7.imprint","IMPRINT",EDGE,{"derivedFrom":sQuery(id+"F7.wireOp",EDGE,"E452")}),1.0]])]});
            var Q3;
            Q3=makeQuery(id+"F7.imprint","IMPRINT",FACE,{"disambiguationData":[TD([[makeQuery(id+"F7.imprint","IMPRINT",EDGE,{"derivedFrom":sQuery(id+"F7.wireOp",EDGE,"E451")}),1.0]])]});
            extrude(context, id + "F9", {"entities" : qUnion([Q0, Q1, Q2, Q3]), "operationType" : NewBodyOperationType.ADD, "oppositeDirection" : true, "depth" : 6 * mm, "offsetDistance" : 25 * mm});
        }
    });
